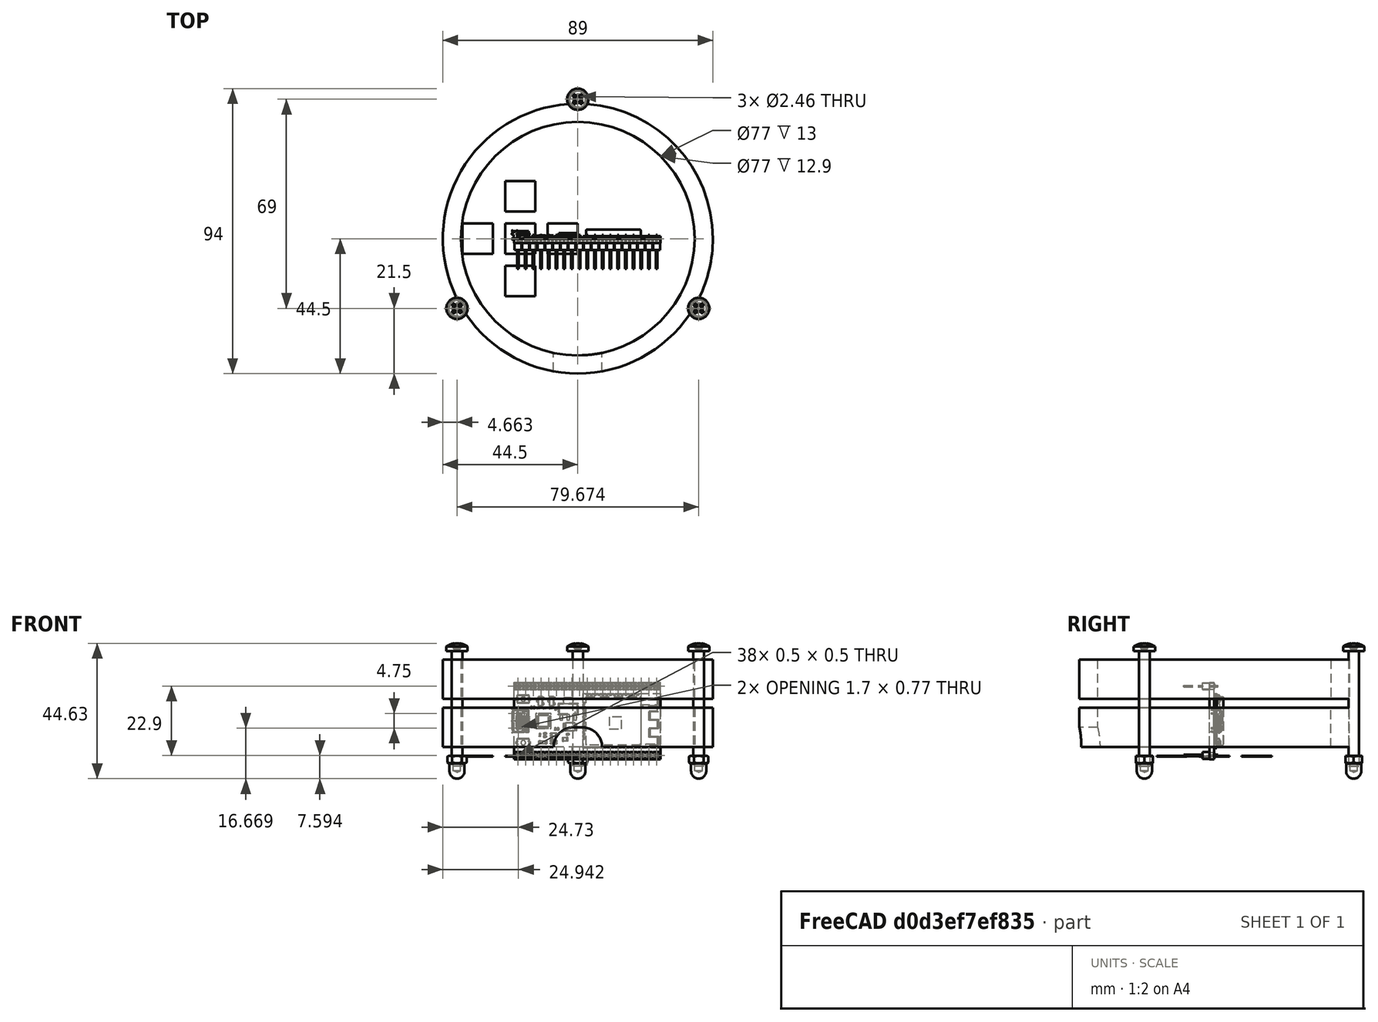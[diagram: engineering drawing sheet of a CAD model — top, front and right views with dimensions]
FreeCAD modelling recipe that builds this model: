
FCSTD DOCUMENT  (FreeCAD 2022.709R28846 (Git))
Label: infinity_02
License: Other
LicenseURL: https://ohwr.org/project/cernohl/wikis/Documents/CERN-OHL-version-2
objects: Part::Feature×98, TechDraw::DrawViewDimension×36, PartDesign::ShapeBinder×12, TechDraw::DrawProjGroupItem×12, Sketcher::SketchObject×10, App::DocumentObjectGroupPython×9, PartDesign::Body×8, TechDraw::DrawHatch×8, PartDesign::Plane×7, PartDesign::Pad×7, TechDraw::DrawSVGTemplate×7, TechDraw::DrawPage×7, TechDraw::DrawViewBalloon×7, Part::FeaturePython×6, TechDraw::DrawProjGroup×6, Part::Part2DObjectPython×4, App::DocumentObjectGroup×3, PartDesign::Pocket×2, Spreadsheet::Sheet×1, Part::Compound2×1, +1 more types
note: 172 computed .brp shape members not serialized (recipe doc carries the construction recipe); baked Part::Feature solids carry a one-line shape summary decoded from their .brp

FEATURE [Spreadsheet::Sheet] Spreadsheet
  PythonMode = false
  ShowCells = 0
  TreeRank = 0
  cells = B1=Enter board size values here manually; C1=NOTES; D1=Micro_Pro; E1=Nano; F1=ESP8266 NodeMCU; G1=ESP32 NodeMCU; H1=Add more boards; I1=Add more boards; A2=Length of the microcontroller board - choose from list (and add more as required); B2(Length)==48mm; D2==34mm; E2==47mm; F2==48mm; G2==48mm; A3=Width of the microcontroller board; B3(width)==26mm; D3==21mm; E3==21mm; F3==26mm; G3==26mm; A4=Screw hole diameter; B4(screw_hole_dia)==3mm; C4=Adds 0.2mm to screw hole diameter; A5=Main Inner circumference; B5(inner_circumference)==240mm; C5=for ESP32 IoT course, make this number divisible by 12 so that 12 LEDs can be placed around circumference for a future clock; A6=Acrylic Thickness; B6(acrylic_thickness)==2.9mm; A7=LED strip width; B7(led_strip_width)==10mm; C7=use this to adjust the height of the upper spacer
FEATURE [Sketcher::SketchObject] Sketch005
  ArcFitTolerance = 0
  AttachmentSupport = -> [XY_Plane010]
  FullyConstrained = true
  MapMode = 5
  Support = -> [XY_Plane010]
  TreeRank = 0
  expr: Constraints[1] = Spreadsheet.inner_circumference / 3.14159
  sketch-geometry (53):
    g0: Circle CenterX=0 CenterY=0 CenterZ=0 NormalX=0 NormalY=0 NormalZ=1 AngleXU=0 Radius=38.1972
    g1: Circle CenterX=0 CenterY=0 CenterZ=0 NormalX=0 NormalY=0 NormalZ=1 AngleXU=0 Radius=44.5
    g2: Circle CenterX=0 CenterY=0 CenterZ=0 NormalX=0 NormalY=0 NormalZ=1 AngleXU=0 Radius=50
    g3: Circle CenterX=0 CenterY=0 CenterZ=0 NormalX=0 NormalY=0 NormalZ=1 AngleXU=0 Radius=38.5
    g4: LineSegment StartX=38.2587 StartY=9.99981 StartZ=0 EndX=28.1331 EndY=27.7894 EndZ=0
    g5: LineSegment StartX=28.1331 StartY=27.7894 StartZ=0 EndX=10.4692 EndY=38.1329 EndZ=0
    g6: LineSegment StartX=10.4692 StartY=38.1329 StartZ=0 EndX=-9.99981 EndY=38.2587 EndZ=0
    g7: LineSegment StartX=-9.99981 StartY=38.2587 StartZ=0 EndX=-27.7894 EndY=28.1331 EndZ=0
    g8: LineSegment StartX=-27.7894 StartY=28.1331 StartZ=0 EndX=-38.1329 EndY=10.4692 EndZ=0
    g9: LineSegment StartX=-38.1329 StartY=10.4692 StartZ=0 EndX=-38.2587 EndY=-9.99981 EndZ=0
    g10: LineSegment StartX=-38.2587 StartY=-9.99981 StartZ=0 EndX=-28.1331 EndY=-27.7894 EndZ=0
    g11: LineSegment StartX=-28.1331 StartY=-27.7894 StartZ=0 EndX=-10.4692 EndY=-38.1329 EndZ=0
    g12: LineSegment StartX=-10.4692 StartY=-38.1329 StartZ=0 EndX=9.99981 EndY=-38.2587 EndZ=0
    g13: LineSegment StartX=9.99981 StartY=-38.2587 StartZ=0 EndX=27.7894 EndY=-28.1331 EndZ=0
    g14: LineSegment StartX=27.7894 StartY=-28.1331 StartZ=0 EndX=38.1329 EndY=-10.4692 EndZ=0
    g15: LineSegment StartX=38.1329 StartY=-10.4692 StartZ=0 EndX=38.2587 EndY=9.99981 EndZ=0
    g16: Circle [constr] CenterX=0 CenterY=0 CenterZ=0 NormalX=0 NormalY=0 NormalZ=1 AngleXU=0 Radius=39.5439
    g17: LineSegment StartX=0 StartY=0 StartZ=0 EndX=0 EndY=38.1972 EndZ=0
    g18: LineSegment StartX=0 StartY=0 StartZ=0 EndX=19.0986 EndY=33.0798 EndZ=0
    g19: LineSegment StartX=0 StartY=0 StartZ=0 EndX=33.0798 EndY=19.0986 EndZ=0
    g20: LineSegment StartX=0 StartY=0 StartZ=0 EndX=38.1972 EndY=3.5e-15 EndZ=0
    g21: LineSegment StartX=0 StartY=0 StartZ=0 EndX=33.0798 EndY=-19.0986 EndZ=0
    g22: LineSegment StartX=0 StartY=0 StartZ=0 EndX=19.0986 EndY=-33.0798 EndZ=0
    g23: LineSegment StartX=0 StartY=0 StartZ=0 EndX=1.85e-14 EndY=-38.1972 EndZ=0
    g24: LineSegment StartX=0 StartY=0 StartZ=0 EndX=-19.0986 EndY=-33.0798 EndZ=0
    g25: LineSegment StartX=0 StartY=0 StartZ=0 EndX=-33.0798 EndY=-19.0986 EndZ=0
    g26: LineSegment StartX=0 StartY=0 StartZ=0 EndX=-38.1972 EndY=-5.03e-14 EndZ=0
    g27: LineSegment StartX=0 StartY=0 StartZ=0 EndX=-33.0798 EndY=19.0986 EndZ=0
    g28: LineSegment StartX=0 StartY=0 StartZ=0 EndX=-19.0986 EndY=33.0798 EndZ=0
    g29: LineSegment StartX=0 StartY=0 StartZ=0 EndX=3.99992 EndY=38.1726 EndZ=0
    g30: LineSegment StartX=0 StartY=0 StartZ=0 EndX=-3.99992 EndY=38.2218 EndZ=0
    g31: LineSegment StartX=0 StartY=0 StartZ=0 EndX=15.6469 EndY=35.101 EndZ=0
    g32: LineSegment StartX=0 StartY=0 StartZ=0 EndX=22.5504 EndY=31.0585 EndZ=0
    g33: LineSegment StartX=0 StartY=0 StartZ=0 EndX=31.1011 EndY=22.5749 EndZ=0
    g34: LineSegment StartX=0 StartY=0 StartZ=0 EndX=35.0584 EndY=15.6223 EndZ=0
    g35: LineSegment StartX=0 StartY=0 StartZ=0 EndX=38.2218 EndY=3.99992 EndZ=0
    g36: LineSegment StartX=0 StartY=0 StartZ=0 EndX=38.1726 EndY=-3.99992 EndZ=0
    g37: LineSegment StartX=0 StartY=0 StartZ=0 EndX=35.101 EndY=-15.6469 EndZ=0
    g38: LineSegment StartX=0 StartY=0 StartZ=0 EndX=31.0585 EndY=-22.5504 EndZ=0
    g39: LineSegment StartX=0 StartY=0 StartZ=0 EndX=22.5749 EndY=-31.1011 EndZ=0
    g40: LineSegment StartX=0 StartY=0 StartZ=0 EndX=15.6223 EndY=-35.0584 EndZ=0
    g41: LineSegment StartX=0 StartY=0 StartZ=0 EndX=3.99992 EndY=-38.2218 EndZ=0
    g42: LineSegment StartX=0 StartY=0 StartZ=0 EndX=-3.99992 EndY=-38.1726 EndZ=0
    g43: LineSegment StartX=0 StartY=0 StartZ=0 EndX=-15.6469 EndY=-35.101 EndZ=0
    g44: LineSegment StartX=0 StartY=0 StartZ=0 EndX=-22.5504 EndY=-31.0585 EndZ=0
    g45: LineSegment StartX=0 StartY=0 StartZ=0 EndX=-31.1011 EndY=-22.5749 EndZ=0
    g46: LineSegment StartX=0 StartY=0 StartZ=0 EndX=-35.0584 EndY=-15.6223 EndZ=0
    g47: LineSegment StartX=0 StartY=0 StartZ=0 EndX=-38.2218 EndY=-3.99992 EndZ=0
    g48: LineSegment StartX=0 StartY=0 StartZ=0 EndX=-38.1726 EndY=3.99992 EndZ=0
    g49: LineSegment StartX=0 StartY=0 StartZ=0 EndX=-35.101 EndY=15.6469 EndZ=0
    g50: LineSegment StartX=0 StartY=0 StartZ=0 EndX=-31.0585 EndY=22.5504 EndZ=0
    g51: LineSegment StartX=0 StartY=0 StartZ=0 EndX=-22.5749 EndY=31.1011 EndZ=0
    g52: LineSegment StartX=0 StartY=0 StartZ=0 EndX=-15.6223 EndY=35.0584 EndZ=0
  constraints (143):
    c: Coincident(g0,g-1)
    c: Diameter(g0) = 76.3944
    c: Coincident(g1,g0)
    c: Diameter(g1) = 89
    c: Coincident(g2,g0)
    c: Diameter(g2) = 100
    c: Coincident(g3,g0)
    c: Diameter(g3) = 77
    c: Coincident(g4,g5)
    c: Coincident(g5,g6)
    c: Coincident(g6,g7)
    c: Coincident(g7,g8)
    c: Coincident(g8,g9)
    c: Coincident(g9,g10)
    c: Coincident(g10,g11)
    c: Coincident(g11,g12)
    c: Coincident(g12,g13)
    c: Coincident(g13,g14)
    c: Coincident(g14,g15)
    c: Coincident(g15,g4)
    c: Equal(g4, g5-g15) x11
    c: PointOnObject(g4,g16)
    c: PointOnObject(g5,g16)
    c: PointOnObject(g6,g16)
    c: PointOnObject(g7,g16)
    c: PointOnObject(g8,g16)
    c: PointOnObject(g9,g16)
    c: PointOnObject(g10,g16)
    c: PointOnObject(g11,g16)
    c: PointOnObject(g12,g16)
    c: PointOnObject(g13,g16)
    c: PointOnObject(g14,g16)
    c: Coincident(g16,g0)
    c: Coincident(g17,g0)
    c: PointOnObject(g17,g6)
    c: Distance(g17,g6) = 10
    c: Coincident(g18,g0)
    c: PointOnObject(g18,g5)
    c: Coincident(g19,g0)
    c: PointOnObject(g19,g4)
    c: Coincident(g20,g0)
    c: PointOnObject(g20,g15)
    c: Coincident(g21,g0)
    c: PointOnObject(g21,g14)
    c: Coincident(g22,g0)
    c: PointOnObject(g22,g13)
    c: Coincident(g23,g0)
    c: PointOnObject(g23,g12)
    c: Coincident(g24,g0)
    c: PointOnObject(g24,g11)
    c: Coincident(g25,g0)
    c: PointOnObject(g25,g10)
    c: Coincident(g26,g0)
    c: PointOnObject(g26,g9)
    c: Coincident(g27,g0)
    c: PointOnObject(g27,g8)
    c: Coincident(g28,g0)
    c: PointOnObject(g28,g7)
    c: Angle(g18,g17) = 0.523599
    c: Angle(g19,g18) = 0.523599
    c: Angle(g20,g19) = 0.523599
    c: Angle(g21,g20) = 0.523599
    c: Angle(g22,g21) = 0.523599
    c: Angle(g23,g22) = 0.523599
    c: Angle(g24,g23) = 0.523599
    c: Angle(g25,g24) = 0.523599
    c: Angle(g26,g25) = 0.523599
    c: Angle(g27,g26) = 0.523599
    c: Angle(g28,g27) = 0.523599
    c: PointOnObject(g4,g16)
    c: Vertical(g17)
    c: PointOnObject(g17,g0)
    c: Coincident(g29,g0)
    c: PointOnObject(g29,g6)
    c: Coincident(g30,g0)
    c: Symmetric(g30,g29,g17)
    c: Distance(g29,g30) = 8
    c: Coincident(g31,g0)
    c: PointOnObject(g31,g5)
    c: Coincident(g32,g0)
    c: PointOnObject(g32,g5)
    c: Angle(g31,g30) = 0.523599
    c: Angle(g32,g29) = 0.523599
    c: Coincident(g33,g0)
    c: PointOnObject(g33,g4)
    c: Coincident(g34,g0)
    c: PointOnObject(g34,g4)
    c: Angle(g33,g31) = 0.523599
    c: Angle(g34,g32) = 0.523599
    c: Coincident(g35,g0)
    c: PointOnObject(g35,g15)
    c: Coincident(g36,g0)
    c: PointOnObject(g36,g15)
    c: Angle(g35,g33) = 0.523599
    c: Angle(g36,g34) = 0.523599
    c: Coincident(g37,g0)
    c: PointOnObject(g37,g14)
    c: Coincident(g38,g0)
    c: PointOnObject(g38,g14)
    c: Angle(g37,g35) = 0.523599
    c: Angle(g38,g36) = 0.523599
    c: Coincident(g39,g0)
    c: PointOnObject(g39,g13)
    c: Coincident(g40,g0)
    c: PointOnObject(g40,g13)
    c: Angle(g39,g37) = 0.523599
    c: Angle(g40,g38) = 0.523599
    c: Coincident(g41,g0)
    c: PointOnObject(g41,g12)
    c: Coincident(g42,g0)
    c: PointOnObject(g42,g12)
    c: Angle(g41,g39) = 0.523599
    c: Angle(g42,g40) = 0.523599
    c: Coincident(g43,g0)
    c: PointOnObject(g43,g11)
    c: Coincident(g44,g0)
    c: PointOnObject(g44,g11)
    c: Angle(g43,g41) = 0.523599
    c: Angle(g44,g42) = 0.523599
    c: Coincident(g45,g0)
    c: PointOnObject(g45,g10)
    c: Coincident(g46,g0)
    c: PointOnObject(g46,g10)
    c: Angle(g45,g43) = 0.523599
    c: Angle(g46,g44) = 0.523599
    c: Coincident(g47,g0)
    c: PointOnObject(g47,g9)
    c: Coincident(g48,g0)
    c: PointOnObject(g48,g9)
    c: Angle(g47,g45) = 0.523599
    c: Angle(g48,g46) = 0.523599
    c: Coincident(g49,g0)
    c: PointOnObject(g49,g8)
    c: Coincident(g50,g0)
    c: PointOnObject(g50,g8)
    c: Angle(g49,g47) = 0.523599
    c: Angle(g50,g48) = 0.523599
    c: Coincident(g51,g0)
    c: PointOnObject(g51,g7)
    c: Coincident(g52,g0)
    c: PointOnObject(g52,g7)
    c: Angle(g51,g49) = 0.523599
    c: Angle(g52,g50) = 0.523599
FEATURE [PartDesign::Body] Body010
  AutoGroupSolids = false
  ClaimAllChildren = false
  ExportMode = 0
  Group = -> [Sketch005]
  Origin = -> Origin013
  TreeRank = 0
  _ExportChildren = -> [Sketch005]
  _GroupVersion = 1
FEATURE [PartDesign::ShapeBinder] ShapeBinder
  Support = -> [Sketch005]
  TraceSupport = false
  TreeRank = 0
FEATURE [PartDesign::Plane] DatumPlane
  AttachmentSupport = -> [ShapeBinder]
  Length = 10
  MapMode = 11
  MinimumLength = 10
  MinimumWidth = 10
  Placement = pos=(0,0,0) rot=(0,0,1;1.5708rad)
  ResizeMode = 0
  Support = -> [ShapeBinder]
  TreeRank = 0
  Width = 10
FEATURE [Sketcher::SketchObject] Sketch
  ArcFitTolerance = 0
  AttachmentSupport = -> [DatumPlane]
  ExternalGeometry = -> [ShapeBinder]
  FullyConstrained = true
  MapMode = 5
  Placement = pos=(0,0,0) rot=(0,0,1;1.5708rad)
  Support = -> [DatumPlane]
  TreeRank = 0
  sketch-geometry (2):
    g0: Circle CenterX=0 CenterY=0 CenterZ=0 NormalX=0 NormalY=0 NormalZ=1 AngleXU=0 Radius=44.5
    g1: Circle CenterX=0 CenterY=0 CenterZ=0 NormalX=0 NormalY=0 NormalZ=1 AngleXU=0 Radius=38.5
  constraints (4):
    c: Coincident(g0,g-4)
    c: Coincident(g1,g0)
    c: Equal(g1,g-4)
    c: Equal(g-3,g0)
FEATURE [PartDesign::Pad] Pad
  ClaimChildren = false
  Direction = (1,1,1)
  Fit = 0
  FitJoin = 0
  InnerFit = 0
  InnerFitJoin = 0
  InnerTaperAngle = 0
  InnerTaperAngleRev = 0
  Length = 5
  Length2 = 8
  NewSolid = false
  Placement = pos=(0,0,0) rot=(0,0,1;1.5708rad)
  Profile = -> Sketch
  Reversed = true
  Suppress = false
  TreeRank = 0
  Type = 4
  _ProfileBasedVersion = 0
FEATURE [PartDesign::Plane] DatumPlane002
  AttachmentOffset = pos=(0,0,0) rot=(1,0,0;1.5708rad)
  AttachmentSupport = -> [Pad]
  Length = 89
  MapMode = 45
  MinimumLength = 10
  MinimumWidth = 10
  Placement = pos=(3e-16,-1.42e-14,-1.5) rot=(1,0,0;1.5708rad)
  ResizeMode = 0
  Support = -> [Pad]
  TreeRank = 0
  Width = 13
FEATURE [Sketcher::SketchObject] Sketch007
  ArcFitTolerance = 0
  AttachmentSupport = -> [DatumPlane002]
  ExternalGeometry = -> [Pad]
  FullyConstrained = true
  MapMode = 5
  Placement = pos=(3e-16,-1.42e-14,-1.5) rot=(1,0,0;1.5708rad)
  Support = -> [DatumPlane002]
  TreeRank = 0
  sketch-geometry (4):
    g0: ArcOfCircle CenterX=-1.5 CenterY=-6.5 CenterZ=0 NormalX=0 NormalY=0 NormalZ=1 AngleXU=0 Radius=6.5 StartAngle=1.5708 EndAngle=4.71239
    g1: ArcOfCircle CenterX=1.5 CenterY=-6.5 CenterZ=0 NormalX=0 NormalY=0 NormalZ=1 AngleXU=0 Radius=6.5 StartAngle=4.71239 EndAngle=7.85398
    g2: LineSegment StartX=-1.5 StartY=-13 StartZ=0 EndX=1.5 EndY=-13 EndZ=0
    g3: LineSegment StartX=-1.5 StartY=9e-16 StartZ=0 EndX=1.5 EndY=1.8e-15 EndZ=0
  constraints (9):
    c: Tangent(g0,g3) = 1.5708
    c: Tangent(g0,g2) = -1.5708
    c: Tangent(g2,g1) = -1.5708
    c: Tangent(g3,g1) = 1.5708
    c: Horizontal(g2)
    c: DistanceX(g0,g1) = 3
    c: Symmetric(g1,g0,g-2)
    c: Radius(g0) = 6.5
    c: PointOnObject(g0,g-3)
FEATURE [PartDesign::Pocket] Pocket
  BaseFeature = -> Pad
  ClaimChildren = false
  Fit = 0
  FitJoin = 0
  InnerFit = 0
  InnerFitJoin = 0
  InnerTaperAngle = 0
  InnerTaperAngleRev = 0
  Length = 26
  Length2 = 100
  NewSolid = false
  Placement = pos=(0,0,0) rot=(0,0,1;1.5708rad)
  Profile = -> Sketch007
  Reversed = true
  Suppress = false
  TreeRank = 0
  Type = 1
  _ProfileBasedVersion = 0
FEATURE [PartDesign::Body] Body  label="PCB_lower_spacer"
  AutoGroupSolids = false
  ClaimAllChildren = false
  ExportMode = 0
  Group = -> [ShapeBinder,DatumPlane,Sketch,Pad,DatumPlane002,Sketch007,Pocket]
  Origin = -> Origin
  Tip = -> Pocket
  TreeRank = 0
  _ExportChildren = -> [ShapeBinder,DatumPlane,Pad,DatumPlane002,Pocket]
  _GroupVersion = 1
FEATURE [PartDesign::ShapeBinder] ShapeBinder002
  Support = -> [Sketch005]
  TraceSupport = false
  TreeRank = 0
FEATURE [PartDesign::ShapeBinder] ShapeBinder003
  Support = -> [Body]
  TraceSupport = false
  TreeRank = 0
FEATURE [PartDesign::Plane] DatumPlane004
  AttachmentSupport = -> [ShapeBinder003]
  Length = 100
  MapMode = 5
  MinimumLength = 10
  MinimumWidth = 10
  Placement = pos=(0,0,5) rot=(0,0,1;0rad)
  ResizeMode = 0
  Support = -> [ShapeBinder003]
  TreeRank = 0
  Width = 99.9333
FEATURE [Sketcher::SketchObject] Sketch009
  ArcFitTolerance = 0
  AttachmentSupport = -> [DatumPlane004]
  ExternalGeometry = -> [ShapeBinder002]
  FullyConstrained = true
  MapMode = 5
  Placement = pos=(0,0,5) rot=(0,0,1;0rad)
  Support = -> [DatumPlane004]
  TreeRank = 0
  expr: Constraints[1] = Spreadsheet.screw_hole_dia
  sketch-geometry (8):
    g0: Circle CenterX=0 CenterY=0 CenterZ=0 NormalX=0 NormalY=0 NormalZ=1 AngleXU=0 Radius=50
    g1: Circle CenterX=0 CenterY=46 CenterZ=0 NormalX=0 NormalY=0 NormalZ=1 AngleXU=0 Radius=1.5
    g2: Circle CenterX=-39.8372 CenterY=-23 CenterZ=0 NormalX=0 NormalY=0 NormalZ=1 AngleXU=0 Radius=1.5
    g3: Circle CenterX=39.8372 CenterY=-23 CenterZ=0 NormalX=0 NormalY=0 NormalZ=1 AngleXU=0 Radius=1.5
    g4: LineSegment [constr] StartX=0 StartY=46 StartZ=0 EndX=-39.8372 EndY=-23 EndZ=0
    g5: LineSegment [constr] StartX=-39.8372 StartY=-23 StartZ=0 EndX=39.8372 EndY=-23 EndZ=0
    g6: LineSegment [constr] StartX=39.8372 StartY=-23 StartZ=0 EndX=0 EndY=46 EndZ=0
    g7: Circle [constr] CenterX=0 CenterY=0 CenterZ=0 NormalX=0 NormalY=0 NormalZ=1 AngleXU=0 Radius=46
  constraints (19):
    c: Equal(g-3,g0)
    c: Diameter(g1) = 3
    c: Equal(g1,g2)
    c: Equal(g1,g3)
    c: PointOnObject(g1,g-2)
    c: Tangent(g1,g-5)
    c: Tangent(g2,g-5)
    c: Tangent(g3,g-5)
    c: Coincident(g4,g5)
    c: Coincident(g5,g6)
    c: Coincident(g6,g4)
    c: Equal(g4,g5)
    c: Equal(g4,g6)
    c: PointOnObject(g4,g7)
    c: Coincident(g6,g1)
    c: Coincident(g2,g4)
    c: Coincident(g3,g5)
    c: Coincident(g0,g-5)
    c: Coincident(g7,g0)
FEATURE [PartDesign::Pad] Pad002
  ClaimChildren = false
  Direction = (1,1,1)
  Fit = 0
  FitJoin = 0
  InnerFit = 0
  InnerFitJoin = 0
  InnerTaperAngle = 0
  InnerTaperAngleRev = 0
  Length = 2.9
  Length2 = 100
  NewSolid = false
  Placement = pos=(0,0,5) rot=(0,0,1;0rad)
  Profile = -> Sketch009
  Suppress = false
  TreeRank = 0
  Type = 0
  _ProfileBasedVersion = 0
  expr: Length = Spreadsheet.acrylic_thickness
FEATURE [Part::Feature] Solid089
  TreeRank = 0
  shape: bbox 0.66 x 0.051 x 0.304 mm, 6 faces (baked)
FEATURE [Part::Feature] Solid090
  TreeRank = 0
  shape: bbox 0.5016 x 0.5016 x 1 mm, 66 faces (baked)
FEATURE [Part::Feature] Solid091
  TreeRank = 0
  shape: bbox 0.66 x 0.051 x 0.304 mm, 6 faces (baked)
FEATURE [Part::Feature] Solid092
  TreeRank = 0
  shape: bbox 0.66 x 0.051 x 0.304 mm, 6 faces (baked)
FEATURE [Part::Feature] Solid093
  TreeRank = 0
  shape: bbox 1.02 x 0.52 x 0.52 mm, 15 faces (baked)
FEATURE [Part::Feature] Solid094
  TreeRank = 0
  shape: bbox 0.65 x 1.325 x 2.3 mm, 11 faces (baked)
FEATURE [Part::Feature] Solid095
  TreeRank = 0
  shape: bbox 2.126 x 0.2178 x 1.073 mm, 52 faces (baked)
FEATURE [Part::Feature] Solid096
  TreeRank = 0
  shape: bbox 0.4 x 0.2 x 0.8 mm, 8 faces (baked)
FEATURE [Part::Feature] Solid097
  TreeRank = 0
  shape: bbox 4.2 x 1.55 x 0.3 mm, 15 faces (baked)
FEATURE [Part::Feature] Solid098
  TreeRank = 0
  shape: bbox 1.624 x 0.5 x 1.624 mm, 6 faces (baked)
FEATURE [Part::Feature] Solid099
  TreeRank = 0
  shape: bbox 1.02 x 0.52 x 0.52 mm, 15 faces (baked)
FEATURE [Part::Feature] Solid100
  TreeRank = 0
  shape: bbox 1 x 0.5016 x 0.5016 mm, 66 faces (baked)
FEATURE [Part::Feature] Solid101
  TreeRank = 0
  shape: bbox 3.9 x 1.7 x 2.5 mm, 6 faces (baked)
FEATURE [Part::Feature] Solid102
  TreeRank = 0
  shape: bbox 0.4 x 0.2 x 0.8 mm, 8 faces (baked)
FEATURE [Part::Feature] Solid103
  TreeRank = 0
  shape: bbox 4.2 x 1.55 x 0.3 mm, 15 faces (baked)
FEATURE [Part::Feature] Solid104
  TreeRank = 0
  shape: bbox 4.2 x 1.55 x 0.3 mm, 15 faces (baked)
FEATURE [Part::Feature] Solid105
  TreeRank = 0
  shape: bbox 1 x 0.5016 x 0.5016 mm, 66 faces (baked)
FEATURE [Part::Feature] Solid106
  TreeRank = 0
  shape: bbox 6.707 x 1.804 x 3.709 mm, 14 faces (baked)
FEATURE [Part::Feature] Solid107
  TreeRank = 0
  shape: bbox 0.52 x 0.52 x 1.02 mm, 15 faces (baked)
FEATURE [Part::Feature] Solid108
  TreeRank = 0
  shape: bbox 2 x 0.8516 x 1.252 mm, 66 faces (baked)
FEATURE [Part::Feature] Solid109
  TreeRank = 0
  shape: bbox 1.624 x 0.5 x 1.624 mm, 6 faces (baked)
FEATURE [Part::Feature] Solid110
  TreeRank = 0
  shape: bbox 3.9 x 1.2 x 0.1 mm, 14 faces (baked)
FEATURE [Part::Feature] Solid111
  TreeRank = 0
  shape: bbox 0.8392 x 0.9032 x 1.792 mm, 14 faces (baked)
FEATURE [Part::Feature] Solid112
  TreeRank = 0
  shape: bbox 3.9 x 1.7 x 2.5 mm, 6 faces (baked)
FEATURE [Part::Feature] Solid113
  TreeRank = 0
  shape: bbox 2.5 x 1.11 x 3 mm, 49 faces (baked)
FEATURE [Part::Feature] Solid114
  TreeRank = 0
  shape: bbox 0.304 x 0.051 x 0.66 mm, 6 faces (baked)
FEATURE [Part::Feature] Solid115
  TreeRank = 0
  shape: bbox 1.333 x 0.3705 x 1.073 mm, 18 faces (baked)
FEATURE [Part::Feature] Solid116 .. Solid121  x6 (patterned run collapsed; names and placements below)
  TreeRank = 0
  shape: bbox 0.304 x 0.051 x 0.66 mm, 6 faces (baked)
FEATURE [Part::Feature] Solid122
  TreeRank = 0
  shape: bbox 0.66 x 0.051 x 0.304 mm, 6 faces (baked)
FEATURE [Part::Feature] Solid123
  TreeRank = 0
  shape: bbox 0.52 x 0.52 x 1.02 mm, 15 faces (baked)
FEATURE [Part::Feature] Solid124
  TreeRank = 0
  shape: bbox 0.66 x 0.051 x 0.304 mm, 6 faces (baked)
FEATURE [Part::Feature] Solid125
  TreeRank = 0
  shape: bbox 3.9 x 1.2 x 0.1 mm, 14 faces (baked)
FEATURE [Part::Feature] Solid126 .. Solid130  x5 (patterned run collapsed; names and placements below)
  TreeRank = 0
  shape: bbox 0.66 x 0.051 x 0.304 mm, 6 faces (baked)
FEATURE [Part::Feature] Solid131
  TreeRank = 0
  shape: bbox 4.16 x 2.41 x 6.91 mm, 176 faces (baked)
FEATURE [Part::Feature] Solid132
  TreeRank = 0
  shape: bbox 0.304 x 0.051 x 0.66 mm, 6 faces (baked)
FEATURE [Part::Feature] Solid133
  TreeRank = 0
  shape: bbox 0.4 x 0.2 x 0.8 mm, 8 faces (baked)
FEATURE [Part::Feature] Solid134 .. Solid138  x5 (patterned run collapsed; names and placements below)
  TreeRank = 0
  shape: bbox 0.304 x 0.051 x 0.66 mm, 6 faces (baked)
FEATURE [Part::Feature] Solid139
  TreeRank = 0
  shape: bbox 0.52 x 0.52 x 1.02 mm, 15 faces (baked)
FEATURE [Part::Feature] Solid140
  TreeRank = 0
  shape: bbox 0.304 x 0.051 x 0.66 mm, 6 faces (baked)
FEATURE [Part::Feature] Solid141
  TreeRank = 0
  shape: bbox 3.352 x 0.051 x 3.352 mm, 6 faces (baked)
FEATURE [Part::Feature] Solid142
  TreeRank = 0
  shape: bbox 1.65 x 1.05 x 1.05 mm, 14 faces (baked)
FEATURE [Part::Feature] Solid143
  TreeRank = 0
  shape: bbox 0.4875 x 0.5625 x 0.9375 mm, 11 faces (baked)
FEATURE [Part::Feature] Solid144
  TreeRank = 0
  shape: bbox 0.4 x 0.2 x 0.8 mm, 8 faces (baked)
FEATURE [Part::Feature] Solid145
  TreeRank = 0
  shape: bbox 1.333 x 0.3705 x 1.073 mm, 18 faces (baked)
FEATURE [Part::Feature] Solid146
  TreeRank = 0
  shape: bbox 0.4875 x 0.5625 x 0.9375 mm, 11 faces (baked)
FEATURE [Part::Feature] Solid147
  TreeRank = 0
  shape: bbox 1 x 0.5016 x 0.5016 mm, 66 faces (baked)
FEATURE [Part::Feature] Solid148
  TreeRank = 0
  shape: bbox 0.8392 x 0.9032 x 1.792 mm, 14 faces (baked)
FEATURE [Part::Feature] Solid149
  TreeRank = 0
  shape: bbox 1.02 x 0.52 x 0.52 mm, 15 faces (baked)
FEATURE [Part::Feature] Solid150
  TreeRank = 0
  shape: bbox 3.151 x 0.9032 x 1.792 mm, 14 faces (baked)
FEATURE [Part::Feature] Solid151
  TreeRank = 0
  shape: bbox 3.3 x 1.775 x 2.7 mm, 7 faces (baked)
FEATURE [Part::Feature] Solid152
  TreeRank = 0
  shape: bbox 0.65 x 1.325 x 2.3 mm, 11 faces (baked)
FEATURE [Part::Feature] Solid153
  TreeRank = 0
  shape: bbox 48.28 x 11.27 x 25.42 mm, 1344 faces (baked)
FEATURE [Part::Feature] Solid154
  TreeRank = 0
  shape: bbox 0.1854 x 0.003 x 0.1854 mm, 4 faces (baked)
FEATURE [Part::Feature] Solid155
  TreeRank = 0
  shape: bbox 2.126 x 0.2178 x 1.073 mm, 52 faces (baked)
FEATURE [Part::Feature] Solid156
  TreeRank = 0
  shape: bbox 4.2 x 1.55 x 0.3 mm, 15 faces (baked)
FEATURE [Part::Feature] Solid157
  TreeRank = 0
  shape: bbox 3.9 x 0.1 x 2.5 mm, 30 faces (baked)
FEATURE [Part::Feature] Solid158
  TreeRank = 0
  shape: bbox 0.52 x 0.52 x 1.02 mm, 15 faces (baked)
FEATURE [Part::Feature] Solid159
  TreeRank = 0
  shape: bbox 0.1 x 0.6 x 0.8 mm, 6 faces (baked)
FEATURE [Part::Feature] Solid160
  TreeRank = 0
  shape: bbox 2.5 x 1.11 x 3 mm, 49 faces (baked)
FEATURE [Part::Feature] Solid161
  TreeRank = 0
  shape: bbox 0.1 x 0.6 x 0.8 mm, 6 faces (baked)
FEATURE [Part::Feature] Solid162
  TreeRank = 0
  shape: bbox 3.9 x 1.2 x 0.1 mm, 14 faces (baked)
FEATURE [Part::Feature] Solid163
  TreeRank = 0
  shape: bbox 1.02 x 0.52 x 0.52 mm, 15 faces (baked)
FEATURE [Part::Feature] Solid164
  TreeRank = 0
  shape: bbox 5.63 x 3.797 x 8.183 mm, 257 faces (baked)
FEATURE [Part::Feature] Solid165
  TreeRank = 0
  shape: bbox 3.9 x 0.1 x 2.5 mm, 30 faces (baked)
FEATURE [Part::Feature] Solid166
  TreeRank = 0
  shape: bbox 4.2 x 1.55 x 0.3 mm, 15 faces (baked)
FEATURE [Part::Feature] Solid167
  TreeRank = 0
  shape: bbox 0.1 x 0.6 x 0.8 mm, 6 faces (baked)
FEATURE [Part::Feature] Solid168
  TreeRank = 0
  shape: bbox 0.1 x 0.6 x 0.8 mm, 6 faces (baked)
FEATURE [Part::Feature] Solid169
  TreeRank = 0
  shape: bbox 3.9 x 1.2 x 0.1 mm, 14 faces (baked)
FEATURE [Part::Feature] Solid170
  TreeRank = 0
  shape: bbox 0.52 x 0.52 x 1.02 mm, 15 faces (baked)
FEATURE [Part::Feature] Solid171
  TreeRank = 0
  shape: bbox 0.8392 x 0.9032 x 1.792 mm, 14 faces (baked)
FEATURE [Part::Feature] Solid172
  TreeRank = 0
  shape: bbox 0.2502 x 0.002 x 0.2502 mm, 4 faces (baked)
FEATURE [Part::Feature] Solid173
  TreeRank = 0
  shape: bbox 5.004 x 0.94 x 5.004 mm, 6 faces (baked)
FEATURE [Part::Feature] Solid174
  TreeRank = 0
  shape: bbox 0.66 x 0.051 x 0.304 mm, 6 faces (baked)
FEATURE [Part::Feature] Solid175
  TreeRank = 0
  shape: bbox 25.54 x 3.035 x 18.07 mm, 584 faces (baked)
FEATURE [Part::Feature] Solid176
  TreeRank = 0
  shape: bbox 0.66 x 0.051 x 0.304 mm, 6 faces (baked)
FEATURE [Part::Feature] Solid177
  TreeRank = 0
  shape: bbox 0.66 x 0.051 x 0.304 mm, 6 faces (baked)
FEATURE [Part::Feature] Solid178
  TreeRank = 0
  shape: bbox 0.66 x 0.051 x 0.304 mm, 6 faces (baked)
FEATURE [Part::Compound2] Compound001  label="ESP32Wroom4"
  Links = -> [Solid089,Solid090,Solid091,Solid092,Solid093,Solid094,Solid095,Solid096,Solid097,Solid098,Solid099,Solid100,Solid101,Solid102,Solid103,Solid104,Solid105,Solid106,Solid107,Solid108,Solid109,Solid110,Solid111,Solid112,Solid113,Solid114,Solid115,Solid116,Solid117,Solid118,Solid119,Solid120,Solid121,Solid122,Solid123,Solid124,Solid125,Solid126,Solid127,Solid128,Solid129,Solid130,Solid131,Solid132,+46 more]
  Placement = pos=(0.5,-15,-5) rot=(-0.57735,-0.57735,0.57735;2.0944rad)
  TreeRank = 0
FEATURE [Sketcher::SketchObject] Sketch010
  ArcFitTolerance = 0
  AttachmentSupport = -> [Pad002]
  ExternalGeometry = -> [ShapeBinder002]
  FullyConstrained = true
  MapMode = 5
  Placement = pos=(0,0,7.9) rot=(0,0,1;0rad)
  Support = -> [Pad002]
  TreeRank = 0
  sketch-geometry (5):
    g0: ArcOfCircle CenterX=-4 CenterY=-34.5 CenterZ=0 NormalX=0 NormalY=0 NormalZ=1 AngleXU=0 Radius=2 StartAngle=1.5708 EndAngle=4.71239
    g1: ArcOfCircle CenterX=4 CenterY=-34.5 CenterZ=0 NormalX=0 NormalY=0 NormalZ=1 AngleXU=0 Radius=2 StartAngle=4.71239 EndAngle=7.85398
    g2: LineSegment StartX=-4 StartY=-36.5 StartZ=0 EndX=4 EndY=-36.5 EndZ=0
    g3: LineSegment StartX=-4 StartY=-32.5 StartZ=0 EndX=4 EndY=-32.5 EndZ=0
    g4: LineSegment [constr] StartX=0 StartY=-38.5 StartZ=0 EndX=0 EndY=-36.5 EndZ=0
  constraints (13):
    c: Tangent(g0,g3) = 1.5708
    c: Tangent(g0,g2) = -1.5708
    c: Tangent(g2,g1) = -1.5708
    c: Tangent(g3,g1) = 1.5708
    c: Horizontal(g2)
    c: Diameter(g0) = 4
    c: Symmetric(g0,g1,g-2)
    c: DistanceX(g0,g1) = 8
    c: PointOnObject(g4,g-3)
    c: PointOnObject(g4,g2)
    c: Vertical(g4)
    c: PointOnObject(g4,g-2)
    c: DistanceY(g4,g4) = 2
FEATURE [PartDesign::Pocket] Pocket001
  BaseFeature = -> Pad002
  ClaimChildren = false
  Fit = 0
  FitJoin = 0
  InnerFit = 0
  InnerFitJoin = 0
  InnerTaperAngle = 0
  InnerTaperAngleRev = 0
  Length = 5
  Length2 = 100
  NewSolid = false
  Placement = pos=(0,0,5) rot=(0,0,1;0rad)
  Profile = -> Sketch010
  Suppress = false
  TreeRank = 0
  Type = 1
  _ProfileBasedVersion = 0
FEATURE [PartDesign::Body] Body012  label="Mirror"
  AutoGroupSolids = false
  ClaimAllChildren = false
  ExportMode = 0
  Group = -> [ShapeBinder002,ShapeBinder003,DatumPlane004,Sketch009,Pad002,Sketch010,Pocket001]
  Origin = -> Origin015
  Tip = -> Pocket001
  TreeRank = 0
  _ExportChildren = -> [ShapeBinder002,ShapeBinder003,DatumPlane004,Pad002,Pocket001]
  _GroupVersion = 1
FEATURE [PartDesign::ShapeBinder] ShapeBinder004 .. ShapeBinder007  x4 (patterned run collapsed; names and placements below)
  Support = -> [Sketch005]
  TraceSupport = false
  TreeRank = 0
FEATURE [PartDesign::Plane] DatumPlane008
  AttachmentSupport = -> [Pocket]
  Length = 98.9466
  MapMode = 5
  MinimumLength = 10
  MinimumWidth = 10
  Placement = pos=(0,0,-8) rot=(0.707107,0.707107,0;3.14159rad)
  ResizeMode = 0
  Support = -> [Pocket]
  TreeRank = 0
  Width = 99.95
FEATURE [Sketcher::SketchObject] Sketch014
  ArcFitTolerance = 0
  AttachmentSupport = -> [DatumPlane008]
  ExternalGeometry = -> [ShapeBinder007]
  FullyConstrained = true
  MapMode = 5
  Placement = pos=(0,0,-8) rot=(0.707107,0.707107,0;3.14159rad)
  Support = -> [DatumPlane008]
  TreeRank = 0
  expr: Constraints[2] = Spreadsheet.screw_hole_dia
  sketch-geometry (62):
    g0: ArcOfCircle CenterX=-7e-16 CenterY=7e-16 CenterZ=0 NormalX=0 NormalY=0 NormalZ=1 AngleXU=0 Radius=50 StartAngle=3.35146 EndAngle=9.21491
    g1: Circle CenterX=-23 CenterY=-39.8372 CenterZ=0 NormalX=0 NormalY=0 NormalZ=1 AngleXU=0 Radius=1.5
    g2: Circle CenterX=46 CenterY=0 CenterZ=0 NormalX=0 NormalY=0 NormalZ=1 AngleXU=0 Radius=1.5
    g3: Circle CenterX=-23 CenterY=39.8372 CenterZ=0 NormalX=0 NormalY=0 NormalZ=1 AngleXU=0 Radius=1.5
    g4: LineSegment [constr] StartX=-23 StartY=-39.8372 StartZ=0 EndX=46 EndY=0 EndZ=0
    g5: LineSegment [constr] StartX=46 StartY=0 StartZ=0 EndX=-23 EndY=39.8372 EndZ=0
    g6: LineSegment [constr] StartX=-23 StartY=39.8372 StartZ=0 EndX=-23 EndY=-39.8372 EndZ=0
    g7: Circle [constr] CenterX=-7e-16 CenterY=7e-16 CenterZ=0 NormalX=0 NormalY=0 NormalZ=1 AngleXU=0 Radius=46
    g8: ArcOfCircle CenterX=22 CenterY=0 CenterZ=0 NormalX=0 NormalY=0 NormalZ=1 AngleXU=0 Radius=6 StartAngle=0.523599 EndAngle=5.75959
    g9: ArcOfCircle CenterX=34 CenterY=0 CenterZ=0 NormalX=0 NormalY=0 NormalZ=1 AngleXU=0 Radius=2 StartAngle=4.71239 EndAngle=7.85398
    g10: LineSegment StartX=28.9282 StartY=-2 StartZ=0 EndX=34 EndY=-2 EndZ=0
    g11: LineSegment StartX=28.9282 StartY=2 StartZ=0 EndX=34 EndY=2 EndZ=0
    g12: ArcOfCircle CenterX=28.9282 CenterY=4 CenterZ=0 NormalX=0 NormalY=0 NormalZ=1 AngleXU=0 Radius=2 StartAngle=3.66519 EndAngle=4.71239
    g13: ArcOfCircle CenterX=28.9282 CenterY=-4 CenterZ=0 NormalX=0 NormalY=0 NormalZ=1 AngleXU=0 Radius=2 StartAngle=1.5708 EndAngle=2.61799
    g14: LineSegment [constr] StartX=-5 StartY=7e-16 StartZ=0 EndX=5 EndY=7e-16 EndZ=0
    g15: LineSegment [constr] StartX=5 StartY=7e-16 StartZ=0 EndX=5 EndY=-10 EndZ=0
    g16: LineSegment [constr] StartX=5 StartY=-10 StartZ=0 EndX=-5 EndY=-10 EndZ=0
    g17: LineSegment [constr] StartX=-5 StartY=-10 StartZ=0 EndX=-5 EndY=0 EndZ=0
    g18: LineSegment [constr] StartX=-19 StartY=-14 StartZ=0 EndX=-9 EndY=-14 EndZ=0
    g19: LineSegment [constr] StartX=-9 StartY=-14 StartZ=0 EndX=-9 EndY=-24 EndZ=0
    g20: LineSegment [constr] StartX=-9 StartY=-24 StartZ=0 EndX=-19 EndY=-24 EndZ=0
    g21: LineSegment [constr] StartX=-19 StartY=-24 StartZ=0 EndX=-19 EndY=-14 EndZ=0
    g22: LineSegment [constr] StartX=9 StartY=-14 StartZ=0 EndX=19 EndY=-14 EndZ=0
    g23: LineSegment [constr] StartX=19 StartY=-14 StartZ=0 EndX=19 EndY=-24 EndZ=0
    g24: LineSegment [constr] StartX=19 StartY=-24 StartZ=0 EndX=9 EndY=-24 EndZ=0
    g25: LineSegment [constr] StartX=9 StartY=-24 StartZ=0 EndX=9 EndY=-14 EndZ=0
    g26: LineSegment [constr] StartX=-5 StartY=-14 StartZ=0 EndX=5 EndY=-14 EndZ=0
    g27: LineSegment [constr] StartX=5 StartY=-14 StartZ=0 EndX=5 EndY=-24 EndZ=0
    g28: LineSegment [constr] StartX=5 StartY=-24 StartZ=0 EndX=-5 EndY=-24 EndZ=0
    g29: LineSegment [constr] StartX=-5 StartY=-24 StartZ=0 EndX=-5 EndY=-14 EndZ=0
    g30: LineSegment [constr] StartX=-5 StartY=-28 StartZ=0 EndX=5 EndY=-28 EndZ=0
    g31: LineSegment [constr] StartX=5 StartY=-28 StartZ=0 EndX=5 EndY=-38 EndZ=0
    g32: LineSegment [constr] StartX=5 StartY=-38 StartZ=0 EndX=-5 EndY=-38 EndZ=0
    g33: LineSegment [constr] StartX=-5 StartY=-38 StartZ=0 EndX=-5 EndY=-28 EndZ=0
    g34: LineSegment [constr] StartX=-5 StartY=-10 StartZ=0 EndX=-5 EndY=-14 EndZ=0
    g35: LineSegment [constr] StartX=-5 StartY=-14 StartZ=0 EndX=-9 EndY=-14 EndZ=0
    g36: LineSegment [constr] StartX=5 StartY=-10 StartZ=0 EndX=5 EndY=-14 EndZ=0
    g37: LineSegment [constr] StartX=5 StartY=-14 StartZ=0 EndX=9 EndY=-14 EndZ=0
    g38: LineSegment [constr] StartX=5 StartY=-28 StartZ=0 EndX=5 EndY=-24 EndZ=0
    g39: LineSegment [constr] StartX=5 StartY=-24 StartZ=0 EndX=9 EndY=-24 EndZ=0
    g40: LineSegment [constr] StartX=-5 StartY=-28 StartZ=0 EndX=-5 EndY=-24 EndZ=0
    g41: LineSegment [constr] StartX=-5 StartY=-24 StartZ=0 EndX=-9 EndY=-24 EndZ=0
    g42: LineSegment [constr] StartX=-7 StartY=-12 StartZ=0 EndX=7 EndY=-12 EndZ=0
    g43: LineSegment [constr] StartX=7 StartY=-12 StartZ=0 EndX=7 EndY=-26 EndZ=0
    g44: LineSegment [constr] StartX=7 StartY=-26 StartZ=0 EndX=-7 EndY=-26 EndZ=0
    g45: LineSegment [constr] StartX=-7 StartY=-26 StartZ=0 EndX=-7 EndY=-12 EndZ=0
    g46: LineSegment [constr] StartX=-1.3e-15 StartY=-12 StartZ=0 EndX=-1.3e-15 EndY=-26 EndZ=0
    g47: LineSegment [constr] StartX=7 StartY=-19 StartZ=0 EndX=-7 EndY=-19 EndZ=0
    g48: Circle CenterX=-7 CenterY=-12 CenterZ=0 NormalX=0 NormalY=0 NormalZ=1 AngleXU=0 Radius=1.5
    g49: Circle CenterX=-1.3e-15 CenterY=-12 CenterZ=0 NormalX=0 NormalY=0 NormalZ=1 AngleXU=0 Radius=1.5
    g50: Circle CenterX=7 CenterY=-12 CenterZ=0 NormalX=0 NormalY=0 NormalZ=1 AngleXU=0 Radius=1.5
    g51: Circle CenterX=7 CenterY=-19 CenterZ=0 NormalX=0 NormalY=0 NormalZ=1 AngleXU=0 Radius=1.5
    g52: Circle CenterX=7 CenterY=-26 CenterZ=0 NormalX=0 NormalY=0 NormalZ=1 AngleXU=0 Radius=1.5
    g53: Circle CenterX=-1.3e-15 CenterY=-26 CenterZ=0 NormalX=0 NormalY=0 NormalZ=1 AngleXU=0 Radius=1.5
    g54: Circle CenterX=-7 CenterY=-26 CenterZ=0 NormalX=0 NormalY=0 NormalZ=1 AngleXU=0 Radius=1.5
    g55: Circle CenterX=-7 CenterY=-19 CenterZ=0 NormalX=0 NormalY=0 NormalZ=1 AngleXU=0 Radius=1.5
    g56: ArcOfCircle CenterX=-36.9468 CenterY=1e-16 CenterZ=0 NormalX=0 NormalY=0 NormalZ=1 AngleXU=0 Radius=8 StartAngle=4.71239 EndAngle=7.85398
    g57: LineSegment StartX=-36.9468 StartY=8 StartZ=0 EndX=-46.9468 EndY=8 EndZ=0
    g58: LineSegment StartX=-36.9468 StartY=-8 StartZ=0 EndX=-46.9468 EndY=-8 EndZ=0
    g59: ArcOfCircle CenterX=-46.9468 CenterY=-10 CenterZ=0 NormalX=0 NormalY=0 NormalZ=1 AngleXU=0 Radius=2 StartAngle=1.5708 EndAngle=3.35146
    g60: ArcOfCircle CenterX=-46.9468 CenterY=10 CenterZ=0 NormalX=0 NormalY=0 NormalZ=1 AngleXU=0 Radius=2 StartAngle=2.93172 EndAngle=4.71239
    g61: LineSegment [constr] StartX=34 StartY=0 StartZ=0 EndX=46 EndY=0 EndZ=0
  constraints (155):
    c: Coincident(g0,g-3)
    c: Equal(g0,g-3)
    c: Diameter(g3) = 3
    c: Equal(g3,g2)
    c: Equal(g3,g1)
    c: Tangent(g1,g-4)
    c: Coincident(g4,g5)
    c: Coincident(g5,g6)
    c: Coincident(g6,g4)
    c: Equal(g4,g5)
    c: Equal(g4,g6)
    c: PointOnObject(g5,g7)
    c: Coincident(g6,g1)
    c: Coincident(g2,g4)
    c: Coincident(g3,g5)
    c: Coincident(g7,g0)
    c: Tangent(g10,g9) = -1.5708
    c: Tangent(g11,g9) = 1.5708
    c: Diameter(g9) = 4
    c: Diameter(g8) = 12
    c: Tangent(g8,g12) = 1.5708
    c: Tangent(g11,g12) = -1.5708
    c: Tangent(g8,g13) = 1.5708
    c: Tangent(g10,g13) = 1.5708
    c: Radius(g13) = 2
    c: Equal(g13,g12)
    c: Coincident(g14,g15)
    c: Coincident(g15,g16)
    c: Coincident(g16,g17)
    c: Coincident(g17,g14)
    c: Horizontal(g14)
    c: Horizontal(g16)
    c: Vertical(g15)
    c: Vertical(g17)
    c: Coincident(g18,g19)
    c: Coincident(g19,g20)
    c: Coincident(g20,g21)
    c: Coincident(g21,g18)
    c: Horizontal(g18)
    c: Horizontal(g20)
    c: Vertical(g19)
    c: Vertical(g21)
    c: Coincident(g22,g23)
    c: Coincident(g23,g24)
    c: Coincident(g24,g25)
    c: Coincident(g25,g22)
    c: Horizontal(g22)
    c: Horizontal(g24)
    c: Vertical(g23)
    c: Vertical(g25)
    c: Coincident(g26,g27)
    c: Coincident(g27,g28)
    c: Coincident(g28,g29)
    c: Coincident(g29,g26)
    c: Horizontal(g26)
    c: Horizontal(g28)
    c: Vertical(g27)
    c: Vertical(g29)
    c: Coincident(g30,g31)
    c: Coincident(g31,g32)
    c: Coincident(g32,g33)
    c: Coincident(g33,g30)
    c: Horizontal(g30)
    c: Horizontal(g32)
    c: Vertical(g31)
    c: Vertical(g33)
    c: Equal(g16,g15)
    c: Equal(g19,g20)
    c: Equal(g31,g32)
    c: Equal(g24,g23)
    c: Equal(g27,g28)
    c: Equal(g14,g18)
    c: Equal(g18,g30)
    c: Equal(g30,g22)
    c: Equal(g22,g26)
    c: DistanceX(g14,g14) = 10
    c: Vertical(g16,g26)
    c: Vertical(g28,g30)
    c: Horizontal(g26,g18)
    c: Horizontal(g26,g22)
    c: Coincident(g34,g16)
    c: Coincident(g34,g26)
    c: Coincident(g35,g26)
    c: Coincident(g35,g18)
    c: Coincident(g36,g15)
    c: Coincident(g36,g26)
    c: Coincident(g37,g26)
    c: Coincident(g37,g22)
    c: Coincident(g38,g30)
    c: Coincident(g38,g27)
    c: Coincident(g39,g27)
    c: Coincident(g39,g24)
    c: Coincident(g40,g30)
    c: Coincident(g40,g28)
    c: Coincident(g41,g28)
    c: Coincident(g41,g19)
    c: Equal(g34,g40)
    c: Equal(g35,g37)
    c: Equal(g35,g34)
    c: DistanceX(g35,g35) = 4
    c: Tangent(g2,g-4)
    c: Coincident(g42,g43)
    c: Coincident(g43,g44)
    c: Coincident(g44,g45)
    c: Coincident(g45,g42)
    c: Symmetric(g18,g26,g45)
    c: Symmetric(g26,g22,g43)
    c: Symmetric(g15,g26,g42)
    c: Symmetric(g27,g30,g44)
    c: PointOnObject(g46,g44)
    c: Vertical(g46)
    c: PointOnObject(g47,g45)
    c: Horizontal(g47)
    c: Symmetric(g42,g42,g46)
    c: Symmetric(g42,g43,g47)
    c: Coincident(g48,g42)
    c: Coincident(g49,g46)
    c: Coincident(g50,g42)
    c: Coincident(g51,g47)
    c: Coincident(g52,g43)
    c: Coincident(g53,g46)
    c: Coincident(g54,g44)
    c: Coincident(g55,g47)
    c: Equal(g54,g55)
    c: Equal(g55,g48)
    c: Equal(g48,g49)
    c: Equal(g49,g50)
    c: Equal(g50,g52)
    c: Equal(g52,g53)
    c: Equal(g53,g51)
    c: Diameter(g51) = 3
    c: Tangent(g56,g58) = 1.5708
    c: Tangent(g56,g57) = -1.5708
    c: Diameter(g56) = 16
    c: Tangent(g58,g59) = -1.5708
    c: Tangent(g0,g59) = -1.5708
    c: Tangent(g57,g60) = 1.5708
    c: Tangent(g0,g60) = -1.5708
    c: Radius(g60) = 2
    c: Equal(g60,g59)
    c: Tangent(g3,g-4)
    c: Equal(g11,g10)
    c: Parallel(g10,g11)
    c: Horizontal(g8,g9)
    c: Distance(g8,g9) = 12
    c: Coincident(g61,g9)
    c: PointOnObject(g61,g7)
    c: Horizontal(g61)
    c: Distance(g61) = 12
    c: PointOnObject(g9,g-1)
    c: Symmetric(g14,g14,g0)
    c: Parallel(g57,g58)
    c: Symmetric(g56,g56,g-1)
    c: DistanceX(g57,g57) = 10
    c: Horizontal(g9,g2)
FEATURE [PartDesign::Pad] Pad006
  ClaimChildren = false
  Direction = (1,1,1)
  Fit = 0
  FitJoin = 0
  InnerFit = 0
  InnerFitJoin = 0
  InnerTaperAngle = 0
  InnerTaperAngleRev = 0
  Length = 2.9
  Length2 = 100
  NewSolid = false
  Placement = pos=(0,0,-8) rot=(0.707107,0.707107,0;3.14159rad)
  Profile = -> Sketch014
  Suppress = false
  TreeRank = 0
  Type = 0
  _ProfileBasedVersion = 0
  expr: Length = Spreadsheet.acrylic_thickness
FEATURE [Part::FeaturePython] Screw  label="(M3.5)x38-Screw"  # Fasteners workbench fastener (typed FeaturePython)
  Placement = pos=(-39.8372,-23,23.7) rot=(0,0,1;0rad)
  TreeRank = 0
  baseObject = -> Body015 [Edge12]
  diameter = 5
  invert = false
  leftHanded = false
  length = 11
  lengthCustom = 38
  matchOuter = false
  offset = 0
  thread = false
  type = 40
FEATURE [Part::FeaturePython] Screw001  label="(M3.5)x38-Screw279"  # Fasteners workbench fastener (typed FeaturePython)
  Placement = pos=(39.8372,-23,23.7) rot=(0,0,1;0rad)
  TreeRank = 0
  baseObject = -> Body015 [Edge9]
  diameter = 5
  invert = false
  leftHanded = false
  length = 11
  lengthCustom = 38
  matchOuter = false
  offset = 0
  thread = false
  type = 40
FEATURE [Part::FeaturePython] Screw002  label="(M3.5)x38-Screw280"  # Fasteners workbench fastener (typed FeaturePython)
  Placement = pos=(0,46,23.7) rot=(0,0,1;0rad)
  TreeRank = 0
  baseObject = -> Body015 [Edge15]
  diameter = 5
  invert = false
  leftHanded = false
  length = 11
  lengthCustom = 38
  matchOuter = false
  offset = 0
  thread = false
  type = 40
FEATURE [Part::FeaturePython] Nut  label="M3-Nut"  # Fasteners workbench fastener (typed FeaturePython)
  Placement = pos=(-39.8372,-23,-10.9) rot=(-1,0,0;3.14159rad)
  TreeRank = 0
  baseObject = -> Body016 [Edge69]
  diameter = 1
  invert = false
  leftHanded = false
  matchOuter = false
  offset = 0
  thread = false
  type = 9
FEATURE [Part::FeaturePython] Nut001  label="M3-Nut433"  # Fasteners workbench fastener (typed FeaturePython)
  Placement = pos=(39.8372,-23,-10.9) rot=(-1,0,0;3.14159rad)
  TreeRank = 0
  baseObject = -> Body016 [Edge63]
  diameter = 1
  invert = false
  leftHanded = false
  matchOuter = false
  offset = 0
  thread = false
  type = 9
FEATURE [Part::FeaturePython] Nut002  label="M3-Nut434"  # Fasteners workbench fastener (typed FeaturePython)
  Placement = pos=(1e-14,46,-10.9) rot=(-1,0,0;3.14159rad)
  TreeRank = 0
  baseObject = -> Body016 [Edge66]
  diameter = 1
  invert = false
  leftHanded = false
  matchOuter = false
  offset = 0
  thread = false
  type = 9
FEATURE [PartDesign::ShapeBinder] ShapeBinder008
  Support = -> [Body012]
  TraceSupport = false
  TreeRank = 5
FEATURE [PartDesign::Plane] DatumPlane005
  AttachmentSupport = -> [ShapeBinder008]
  Length = 89
  MapMode = 5
  MinimumLength = 10
  MinimumWidth = 10
  Placement = pos=(0,0,7.9) rot=(0,0,1;0rad)
  ResizeMode = 0
  Support = -> [ShapeBinder008]
  TreeRank = 0
  Width = 89
FEATURE [Sketcher::SketchObject] Sketch011
  ArcFitTolerance = 0
  AttachmentSupport = -> [DatumPlane005]
  ExternalGeometry = -> [ShapeBinder004]
  FullyConstrained = true
  MapMode = 5
  Placement = pos=(0,0,7.9) rot=(0,0,1;0rad)
  Support = -> [DatumPlane005]
  TreeRank = 0
  sketch-geometry (2):
    g0: Circle CenterX=0 CenterY=0 CenterZ=0 NormalX=0 NormalY=0 NormalZ=1 AngleXU=0 Radius=44.5
    g1: Circle CenterX=0 CenterY=0 CenterZ=0 NormalX=0 NormalY=0 NormalZ=1 AngleXU=0 Radius=38.5
  constraints (4):
    c: Coincident(g0,g-4)
    c: Coincident(g1,g0)
    c: Equal(g1,g-4)
    c: Equal(g-3,g0)
FEATURE [PartDesign::Pad] Pad003
  ClaimChildren = false
  Direction = (1,1,1)
  Fit = 0
  FitJoin = 0
  InnerFit = 0
  InnerFitJoin = 0
  InnerTaperAngle = 0
  InnerTaperAngleRev = 0
  Length = 12.9
  Length2 = 100
  NewSolid = false
  Placement = pos=(0,0,7.9) rot=(0,0,1;0rad)
  Profile = -> Sketch011
  Suppress = false
  TreeRank = 0
  Type = 0
  _ProfileBasedVersion = 0
  expr: Length = Spreadsheet.led_strip_width + Spreadsheet.acrylic_thickness
FEATURE [PartDesign::Body] Body013  label="Upper_spacer"
  AutoGroupSolids = false
  ClaimAllChildren = false
  ExportMode = 0
  Group = -> [ShapeBinder004,DatumPlane005,Sketch011,Pad003,ShapeBinder008]
  Origin = -> Origin016
  Tip = -> Pad003
  TreeRank = 0
  _ExportChildren = -> [ShapeBinder004,DatumPlane005,Pad003,ShapeBinder008]
  _GroupVersion = 1
FEATURE [PartDesign::ShapeBinder] ShapeBinder009
  Support = -> [Body013]
  TraceSupport = false
  TreeRank = 6
FEATURE [PartDesign::Plane] DatumPlane006
  AttachmentSupport = -> [ShapeBinder009]
  Length = 77.4
  MapMode = 5
  MinimumLength = 10
  MinimumWidth = 10
  Placement = pos=(0,0,20.8) rot=(0,0,1;0rad)
  ResizeMode = 0
  Support = -> [ShapeBinder009]
  TreeRank = 0
  Width = 77.3484
FEATURE [Sketcher::SketchObject] Sketch012
  ArcFitTolerance = 0
  AttachmentSupport = -> [DatumPlane006]
  ExternalGeometry = -> [ShapeBinder005]
  FullyConstrained = true
  MapMode = 5
  Placement = pos=(0,0,20.8) rot=(0,0,1;0rad)
  Support = -> [DatumPlane006]
  TreeRank = 0
  sketch-geometry (2):
    g0: Circle CenterX=0 CenterY=0 CenterZ=0 NormalX=0 NormalY=0 NormalZ=1 AngleXU=0 Radius=38.7
    g1: LineSegment [constr] StartX=-38.7 StartY=0 StartZ=0 EndX=-38.5 EndY=0 EndZ=0
  constraints (6):
    c: Coincident(g0,g-3)
    c: PointOnObject(g1,g0)
    c: PointOnObject(g1,g-3)
    c: Horizontal(g1)
    c: PointOnObject(g1,g-1)
    c: DistanceX(g1,g1) = 0.2
FEATURE [PartDesign::Pad] Pad004
  ClaimChildren = false
  Direction = (1,1,1)
  Fit = 0
  FitJoin = 0
  InnerFit = 0
  InnerFitJoin = 0
  InnerTaperAngle = 0
  InnerTaperAngleRev = 0
  Length = 2.9
  Length2 = 100
  NewSolid = false
  Placement = pos=(0,0,20.8) rot=(0,0,1;0rad)
  Profile = -> Sketch012
  Reversed = true
  Suppress = false
  TreeRank = 0
  Type = 0
  _ProfileBasedVersion = 0
  expr: Length = Spreadsheet.acrylic_thickness
FEATURE [PartDesign::Body] Body014  label="Mirror_one_way"
  AutoGroupSolids = false
  ClaimAllChildren = false
  ExportMode = 0
  Group = -> [ShapeBinder005,DatumPlane006,Sketch012,Pad004,ShapeBinder009]
  Origin = -> Origin017
  Tip = -> Pad004
  TreeRank = 0
  _ExportChildren = -> [ShapeBinder005,DatumPlane006,Pad004,ShapeBinder009]
  _GroupVersion = 1
FEATURE [PartDesign::ShapeBinder] ShapeBinder010
  Support = -> [Body013]
  TraceSupport = false
  TreeRank = 7
FEATURE [PartDesign::Plane] DatumPlane007
  AttachmentSupport = -> [ShapeBinder010]
  Length = 100
  MapMode = 5
  MinimumLength = 10
  MinimumWidth = 10
  Placement = pos=(0,0,20.8) rot=(0,0,1;0rad)
  ResizeMode = 0
  Support = -> [ShapeBinder010]
  TreeRank = 0
  Width = 99.9333
FEATURE [Sketcher::SketchObject] Sketch013
  ArcFitTolerance = 0
  AttachmentSupport = -> [DatumPlane007]
  ExternalGeometry = -> [ShapeBinder006]
  FullyConstrained = true
  MapMode = 5
  Placement = pos=(0,0,20.8) rot=(0,0,1;0rad)
  Support = -> [DatumPlane007]
  TreeRank = 0
  expr: Constraints[8] = Spreadsheet.screw_hole_dia
  sketch-geometry (10):
    g0: Circle CenterX=0 CenterY=0 CenterZ=0 NormalX=0 NormalY=0 NormalZ=1 AngleXU=0 Radius=50
    g1: Circle CenterX=0 CenterY=0 CenterZ=0 NormalX=0 NormalY=0 NormalZ=1 AngleXU=0 Radius=37
    g2: LineSegment [constr] StartX=-37 StartY=0 StartZ=0 EndX=-38.5 EndY=0 EndZ=0
    g3: Circle CenterX=0 CenterY=46 CenterZ=0 NormalX=0 NormalY=0 NormalZ=1 AngleXU=0 Radius=1.5
    g4: Circle CenterX=-39.8372 CenterY=-23 CenterZ=0 NormalX=0 NormalY=0 NormalZ=1 AngleXU=0 Radius=1.5
    g5: Circle CenterX=39.8372 CenterY=-23 CenterZ=0 NormalX=0 NormalY=0 NormalZ=1 AngleXU=0 Radius=1.5
    g6: LineSegment [constr] StartX=0 StartY=46 StartZ=0 EndX=-39.8372 EndY=-23 EndZ=0
    g7: LineSegment [constr] StartX=-39.8372 StartY=-23 StartZ=0 EndX=39.8372 EndY=-23 EndZ=0
    g8: LineSegment [constr] StartX=39.8372 StartY=-23 StartZ=0 EndX=0 EndY=46 EndZ=0
    g9: Circle [constr] CenterX=0 CenterY=0 CenterZ=0 NormalX=0 NormalY=0 NormalZ=1 AngleXU=0 Radius=46
  constraints (25):
    c: Coincident(g0,g-4)
    c: Coincident(g1,g0)
    c: Equal(g-3,g0)
    c: PointOnObject(g2,g1)
    c: PointOnObject(g2,g-4)
    c: Horizontal(g2)
    c: PointOnObject(g2,g-1)
    c: DistanceX(g2,g2) = 1.5
    c: Diameter(g4) = 3
    c: Equal(g4,g5)
    c: Equal(g4,g3)
    c: PointOnObject(g3,g-2)
    c: Tangent(g3,g-5)
    c: Coincident(g6,g7)
    c: Coincident(g7,g8)
    c: Coincident(g8,g6)
    c: Equal(g6,g7)
    c: Equal(g6,g8)
    c: PointOnObject(g6,g9)
    c: PointOnObject(g7,g9)
    c: PointOnObject(g8,g9)
    c: Coincident(g9,g0)
    c: Coincident(g8,g3)
    c: Coincident(g4,g6)
    c: Coincident(g5,g7)
FEATURE [PartDesign::Pad] Pad005
  ClaimChildren = false
  Direction = (1,1,1)
  Fit = 0
  FitJoin = 0
  InnerFit = 0
  InnerFitJoin = 0
  InnerTaperAngle = 0
  InnerTaperAngleRev = 0
  Length = 2.9
  Length2 = 100
  NewSolid = false
  Placement = pos=(0,0,20.8) rot=(0,0,1;0rad)
  Profile = -> Sketch013
  Suppress = false
  TreeRank = 0
  Type = 0
  _ProfileBasedVersion = 0
  expr: Length = Spreadsheet.acrylic_thickness
FEATURE [PartDesign::Body] Body015  label="Front_bezel"
  AutoGroupSolids = false
  ClaimAllChildren = false
  ExportMode = 0
  Group = -> [ShapeBinder006,DatumPlane007,Sketch013,Pad005,ShapeBinder010]
  Origin = -> Origin018
  Tip = -> Pad005
  TreeRank = 0
  _ExportChildren = -> [ShapeBinder006,DatumPlane007,Pad005,ShapeBinder010]
  _GroupVersion = 1
FEATURE [PartDesign::ShapeBinder] ShapeBinder011
  Support = -> [Body]
  TraceSupport = false
  TreeRank = 8
FEATURE [PartDesign::Body] Body016  label="Back_cover"
  AutoGroupSolids = false
  ClaimAllChildren = false
  ExportMode = 0
  Group = -> [ShapeBinder007,DatumPlane008,Sketch014,Pad006,ShapeBinder011]
  Origin = -> Origin019
  Tip = -> Pad006
  TreeRank = 0
  _ExportChildren = -> [ShapeBinder007,DatumPlane008,Pad006,ShapeBinder011]
  _GroupVersion = 1
FEATURE [Part::Part2DObjectPython] Shape2DView  label="Back_cover_DXF"  # Draft 2D object (typed FeaturePython)
  Base = -> Body016
  FuseArch = false
  HiddenLines = false
  InPlace = true
  Projection = (0,0,1)
  ProjectionMode = 0
  SegmentLength = 0.05
  Tessellation = false
  TreeRank = 9
  VisibleOnly = false
FEATURE [Part::Part2DObjectPython] Shape2DView001  label="Front_bezel_DXF"  # Draft 2D object (typed FeaturePython)
  Base = -> Body015
  FuseArch = false
  HiddenLines = false
  InPlace = true
  Projection = (0,0,1)
  ProjectionMode = 0
  SegmentLength = 0.05
  Tessellation = false
  TreeRank = 10
  VisibleOnly = false
FEATURE [Part::Part2DObjectPython] Shape2DView002  label="Mirror_one_way_DXF"  # Draft 2D object (typed FeaturePython)
  Base = -> Body014
  FuseArch = false
  HiddenLines = false
  InPlace = true
  Projection = (0,0,1)
  ProjectionMode = 0
  SegmentLength = 0.05
  Tessellation = false
  TreeRank = 11
  VisibleOnly = false
FEATURE [Part::Part2DObjectPython] Shape2DView003  label="Mirror_DXF"  # Draft 2D object (typed FeaturePython)
  Base = -> Body012
  FuseArch = false
  HiddenLines = false
  InPlace = true
  Projection = (0,0,1)
  ProjectionMode = 0
  SegmentLength = 0.05
  Tessellation = false
  TreeRank = 12
  VisibleOnly = false
FEATURE [App::DocumentObjectGroup] Group  label="DXF"
  ClaimAllChildren = true
  ExportMode = 1
  Group = -> [Shape2DView,Shape2DView001,Shape2DView002,Shape2DView003]
  TreeRank = 0
  _GroupVersion = 1
FEATURE [TechDraw::DrawSVGTemplate] Template
  EditableTexts = AUTHOR_NAME=Anool J M,DRAWING_TITLE=Lower Spacer,FC-DATE=02/04/2023,FC-REV=REV A,FC-SC=1:1,FC-SH=1 / 8,FC-SI=A4,FREECAD_DRAWING=77 mm ID, 89 mm OD,+3 more (map truncated)
  Height = 210
  Orientation = 1
  TreeRank = 14
  Width = 297
FEATURE [TechDraw::DrawSVGTemplate] Template001
  EditableTexts = AUTHOR_NAME=Anool J M,DRAWING_TITLE=Upper Spacer,FC-DATE=02/04/2023,FC-REV=REV A,FC-SC=1:1,FC-SH=2 / 8,FC-SI=A4,FREECAD_DRAWING=77 mm ID, 89 mm OD,+3 more (map truncated)
  Height = 210
  Orientation = 1
  TreeRank = 21
  Width = 297
FEATURE [TechDraw::DrawProjGroupItem] ProjItem002  label="Front001"
  CoarseView = false
  Direction = (0,0,1)
  Focus = 100
  HardHidden = true
  IsoCount = 0
  IsoHidden = false
  IsoVisible = false
  LockPosition = true
  Perspective = false
  Rotation = 0
  RotationVector = (1,0,0)
  ScaleType = 2
  SeamHidden = false
  SeamVisible = false
  SmoothHidden = false
  SmoothVisible = true
  Source = -> [Body013]
  TreeRank = 24
  Type = 0
  X = 0
  XDirection = (1,0,0)
  Y = 0
FEATURE [TechDraw::DrawProjGroupItem] ProjItem003  label="Bottom001"
  CoarseView = false
  Direction = (0,-1,0)
  Focus = 100
  HardHidden = true
  IsoCount = 0
  IsoHidden = false
  IsoVisible = false
  LockPosition = false
  Perspective = false
  Rotation = 0
  RotationVector = (1,0,0)
  ScaleType = 2
  SeamHidden = false
  SeamVisible = false
  SmoothHidden = false
  SmoothVisible = true
  Source = -> [Body013]
  TreeRank = 26
  Type = 5
  X = 0
  XDirection = (1,0,0)
  Y = 65.95
FEATURE [TechDraw::DrawProjGroup] ProjGroup001
  Anchor = -> ProjItem002
  AutoDistribute = true
  LockPosition = false
  ProjectionType = 0
  Rotation = 0
  ScaleType = 0
  Source = -> [Body013]
  TreeRank = 25
  Views = -> [ProjItem002,ProjItem003]
  X = 152.158
  Y = 100.518
  spacingX = 15
  spacingY = 15
FEATURE [TechDraw::DrawSVGTemplate] Template002
  EditableTexts = AUTHOR_NAME=Anool J M,DRAWING_TITLE=Mirror, 100%,FC-DATE=02/04/2023,FC-REV=REV A,FC-SC=1:1,FC-SH=3 / 8,FC-SI=A4,FREECAD_DRAWING=100 mm OD,+3 more (map truncated)
  Height = 210
  Orientation = 1
  TreeRank = 28
  Width = 297
FEATURE [TechDraw::DrawProjGroupItem] ProjItem004  label="Front002"
  CoarseView = false
  Direction = (0,0,1)
  Focus = 100
  HardHidden = true
  IsoCount = 0
  IsoHidden = false
  IsoVisible = false
  LockPosition = true
  Perspective = false
  Rotation = 0
  RotationVector = (1,0,0)
  ScaleType = 2
  SeamHidden = false
  SeamVisible = false
  SmoothHidden = false
  SmoothVisible = true
  Source = -> [Body012]
  TreeRank = 31
  Type = 0
  X = 0
  XDirection = (1,0,0)
  Y = 0
FEATURE [TechDraw::DrawProjGroupItem] ProjItem005  label="Right"
  CoarseView = false
  Direction = (1,0,1e-16)
  Focus = 100
  HardHidden = true
  IsoCount = 0
  IsoHidden = false
  IsoVisible = false
  LockPosition = false
  Perspective = false
  Rotation = 0
  RotationVector = (1,0,0)
  ScaleType = 2
  SeamHidden = false
  SeamVisible = false
  SmoothHidden = false
  SmoothVisible = true
  Source = -> [Body012]
  TreeRank = 33
  Type = 2
  X = -66.45
  XDirection = (1e-16,0,-1)
  Y = 0
FEATURE [TechDraw::DrawProjGroup] ProjGroup002
  Anchor = -> ProjItem004
  AutoDistribute = true
  LockPosition = false
  ProjectionType = 0
  Rotation = 0
  ScaleType = 0
  Source = -> [Body012]
  TreeRank = 32
  Views = -> [ProjItem004,ProjItem005]
  X = 103.115
  Y = 122.909
  spacingX = 15
  spacingY = 15
FEATURE [TechDraw::DrawSVGTemplate] Template003
  EditableTexts = AUTHOR_NAME=Anool J M,DRAWING_TITLE=Mirror, one way,FC-DATE=02/04/2023,FC-REV=REV A,FC-SC=1:1,FC-SH=4 / 8,FC-SI=A4,FREECAD_DRAWING=77.4 mm dia,+3 more (map truncated)
  Height = 210
  Orientation = 1
  TreeRank = 35
  Width = 297
FEATURE [TechDraw::DrawProjGroupItem] ProjItem006  label="Front003"
  CoarseView = false
  Direction = (0,0,1)
  Focus = 100
  HardHidden = true
  IsoCount = 0
  IsoHidden = false
  IsoVisible = false
  LockPosition = true
  Perspective = false
  Rotation = 0
  RotationVector = (1,0,0)
  ScaleType = 2
  SeamHidden = false
  SeamVisible = false
  SmoothHidden = false
  SmoothVisible = true
  Source = -> [Body014]
  TreeRank = 38
  Type = 0
  X = 0
  XDirection = (1,0,0)
  Y = 0
FEATURE [TechDraw::DrawProjGroupItem] ProjItem007  label="Right001"
  CoarseView = false
  Direction = (1,0,1e-16)
  Focus = 100
  HardHidden = true
  IsoCount = 0
  IsoHidden = false
  IsoVisible = false
  LockPosition = false
  Perspective = false
  Rotation = 0
  RotationVector = (1,0,0)
  ScaleType = 2
  SeamHidden = false
  SeamVisible = false
  SmoothHidden = false
  SmoothVisible = true
  Source = -> [Body014]
  TreeRank = 40
  Type = 2
  X = -55.15
  XDirection = (1e-16,0,-1)
  Y = 0
FEATURE [TechDraw::DrawProjGroup] ProjGroup003
  Anchor = -> ProjItem006
  AutoDistribute = true
  LockPosition = false
  ProjectionType = 0
  Rotation = 0
  ScaleType = 0
  Source = -> [Body014]
  TreeRank = 39
  Views = -> [ProjItem006,ProjItem007]
  X = 96.828
  Y = 129.074
  spacingX = 15
  spacingY = 15
FEATURE [TechDraw::DrawSVGTemplate] Template004
  EditableTexts = AUTHOR_NAME=Anool J M,DRAWING_TITLE=Front bezel,FC-DATE=02/04/2023,FC-REV=REV A,FC-SC=1:1,FC-SH=5 / 8,FC-SI=A4,FREECAD_DRAWING=100 mm OD, 74 mm ID,+3 more (map truncated)
  Height = 210
  Orientation = 1
  TreeRank = 42
  Width = 297
FEATURE [TechDraw::DrawProjGroupItem] ProjItem008  label="Front004"
  CoarseView = false
  Direction = (0,0,1)
  Focus = 100
  HardHidden = true
  IsoCount = 0
  IsoHidden = false
  IsoVisible = false
  LockPosition = true
  Perspective = false
  Rotation = 0
  RotationVector = (1,0,0)
  ScaleType = 2
  SeamHidden = false
  SeamVisible = false
  SmoothHidden = false
  SmoothVisible = true
  Source = -> [Body015]
  TreeRank = 45
  Type = 0
  X = 0
  XDirection = (1,0,0)
  Y = 0
FEATURE [TechDraw::DrawProjGroupItem] ProjItem009  label="Right002"
  CoarseView = false
  Direction = (1,0,1e-16)
  Focus = 100
  HardHidden = true
  IsoCount = 0
  IsoHidden = false
  IsoVisible = false
  LockPosition = false
  Perspective = false
  Rotation = 0
  RotationVector = (1,0,0)
  ScaleType = 2
  SeamHidden = false
  SeamVisible = false
  SmoothHidden = false
  SmoothVisible = true
  Source = -> [Body015]
  TreeRank = 47
  Type = 2
  X = -66.45
  XDirection = (1e-16,0,-1)
  Y = 0
FEATURE [TechDraw::DrawProjGroup] ProjGroup004
  Anchor = -> ProjItem008
  AutoDistribute = true
  LockPosition = false
  ProjectionType = 0
  Rotation = 0
  ScaleType = 0
  Source = -> [Body015]
  TreeRank = 46
  Views = -> [ProjItem008,ProjItem009]
  X = 107.394
  Y = 122.209
  spacingX = 15
  spacingY = 15
FEATURE [TechDraw::DrawSVGTemplate] Template005
  EditableTexts = AUTHOR_NAME=Anool J M,DRAWING_TITLE=Back cover,FC-DATE=02/04/2023,FC-REV=REV A,FC-SC=1:1,FC-SH=6 / 8,FC-SI=A4,FREECAD_DRAWING=100 mm OD,+3 more (map truncated)
  Height = 210
  Orientation = 1
  TreeRank = 49
  Width = 297
FEATURE [TechDraw::DrawProjGroupItem] ProjItem010  label="Front005"
  CoarseView = false
  Direction = (0,0,1)
  Focus = 100
  HardHidden = true
  IsoCount = 0
  IsoHidden = false
  IsoVisible = false
  LockPosition = true
  Perspective = false
  Rotation = 0
  RotationVector = (1,0,0)
  ScaleType = 2
  SeamHidden = false
  SeamVisible = false
  SmoothHidden = false
  SmoothVisible = true
  Source = -> [Body016]
  TreeRank = 52
  Type = 0
  X = 0
  XDirection = (1,0,0)
  Y = 0
FEATURE [TechDraw::DrawProjGroupItem] ProjItem011  label="Right003"
  CoarseView = false
  Direction = (1,0,1e-16)
  Focus = 100
  HardHidden = true
  IsoCount = 0
  IsoHidden = false
  IsoVisible = false
  LockPosition = false
  Perspective = false
  Rotation = 0
  RotationVector = (1,0,0)
  ScaleType = 2
  SeamHidden = false
  SeamVisible = false
  SmoothHidden = false
  SmoothVisible = true
  Source = -> [Body016]
  TreeRank = 54
  Type = 2
  X = -66.45
  XDirection = (1e-16,0,-1)
  Y = 0
FEATURE [TechDraw::DrawProjGroup] ProjGroup005
  Anchor = -> ProjItem010
  AutoDistribute = true
  LockPosition = false
  ProjectionType = 0
  Rotation = 0
  ScaleType = 0
  Source = -> [Body016]
  TreeRank = 53
  Views = -> [ProjItem010,ProjItem011]
  X = 104.78
  Y = 122.454
  spacingX = 15
  spacingY = 15
FEATURE [TechDraw::DrawViewDimension] Dimension004
  Arbitrary = false
  ArbitraryTolerances = false
  EqualTolerance = true
  FormatSpec = ⌀%.1f
  FormatSpecOverTolerance = %+.1f
  FormatSpecUnderTolerance = %+.1f
  Inverted = false
  LockPosition = false
  MeasureType = 1
  OverTolerance = 0
  References2D = -> [ProjItem002]
  Rotation = 0
  ScaleType = 0
  TheoreticalExact = false
  TreeRank = 59
  Type = 5
  UnderTolerance = 0
  X = 63.4264
  Y = 13.8579
FEATURE [TechDraw::DrawViewDimension] Dimension006
  Arbitrary = false
  ArbitraryTolerances = false
  EqualTolerance = true
  FormatSpec = ⌀%.1f
  FormatSpecOverTolerance = %+.1f
  FormatSpecUnderTolerance = %+.1f
  Inverted = false
  LockPosition = false
  MeasureType = 1
  OverTolerance = 0
  References2D = -> [ProjItem002]
  Rotation = 0
  ScaleType = 0
  TheoreticalExact = false
  TreeRank = 61
  Type = 5
  UnderTolerance = 0
  X = 65.5584
  Y = -11.4594
FEATURE [TechDraw::DrawViewDimension] Dimension007
  Arbitrary = false
  ArbitraryTolerances = false
  EqualTolerance = true
  FormatSpec = %.1f
  FormatSpecOverTolerance = %+.1f
  FormatSpecUnderTolerance = %+.1f
  Inverted = false
  LockPosition = false
  MeasureType = 1
  OverTolerance = 0
  References2D = -> [ProjItem003]
  Rotation = 0
  ScaleType = 0
  TheoreticalExact = false
  TreeRank = 62
  Type = 2
  UnderTolerance = 0
  X = 69.114
  Y = -15.3606
FEATURE [TechDraw::DrawPage] Page001
  KeepUpdated = true
  NextBalloonIndex = 1
  ProjectionType = 0
  Template = -> Template001
  TreeRank = 22
  Views = -> [ProjGroup001,Dimension004,Dimension006,Dimension007]
FEATURE [TechDraw::DrawViewDimension] Dimension008
  Arbitrary = false
  ArbitraryTolerances = false
  EqualTolerance = true
  FormatSpec = ⌀%.1f
  FormatSpecOverTolerance = %+.1f
  FormatSpecUnderTolerance = %+.1f
  Inverted = false
  LockPosition = false
  MeasureType = 1
  OverTolerance = 0
  References2D = -> [ProjItem004]
  Rotation = 0
  ScaleType = 0
  TheoreticalExact = false
  TreeRank = 63
  Type = 5
  UnderTolerance = 0
  X = 71.1548
  Y = 26.1168
FEATURE [TechDraw::DrawViewDimension] Dimension010
  Arbitrary = false
  ArbitraryTolerances = false
  EqualTolerance = true
  FormatSpec = ⌀%.1f
  FormatSpecOverTolerance = %+.1f
  FormatSpecUnderTolerance = %+.1f
  Inverted = false
  LockPosition = false
  MeasureType = 1
  OverTolerance = 0
  References2D = -> [ProjItem004]
  Rotation = 0
  ScaleType = 0
  TheoreticalExact = false
  TreeRank = 65
  Type = 5
  UnderTolerance = 0
  X = 24.5151
  Y = -50.5658
FEATURE [TechDraw::DrawViewDimension] Dimension011
  Arbitrary = false
  ArbitraryTolerances = false
  EqualTolerance = true
  FormatSpec = %.1f
  FormatSpecOverTolerance = %+.1f
  FormatSpecUnderTolerance = %+.1f
  Inverted = false
  LockPosition = false
  MeasureType = 1
  OverTolerance = 0
  References2D = -> [ProjItem004]
  Rotation = 0
  ScaleType = 0
  TheoreticalExact = false
  TreeRank = 66
  Type = 1
  UnderTolerance = 0
  X = -34.341
  Y = -50.7876
FEATURE [TechDraw::DrawViewDimension] Dimension013
  Arbitrary = false
  ArbitraryTolerances = false
  EqualTolerance = true
  FormatSpec = %.1f
  FormatSpecOverTolerance = %+.1f
  FormatSpecUnderTolerance = %+.1f
  Inverted = false
  LockPosition = false
  MeasureType = 1
  OverTolerance = 0
  References2D = -> [ProjItem004]
  Rotation = 0
  ScaleType = 0
  TheoreticalExact = false
  TreeRank = 68
  Type = 0
  UnderTolerance = 0
  X = 12.7683
  Y = -13.6254
FEATURE [TechDraw::DrawViewDimension] Dimension014
  Arbitrary = false
  ArbitraryTolerances = false
  EqualTolerance = true
  FormatSpec = %.1f
  FormatSpecOverTolerance = %+.1f
  FormatSpecUnderTolerance = %+.1f
  Inverted = false
  LockPosition = false
  MeasureType = 1
  OverTolerance = 0
  References2D = -> [ProjItem005]
  Rotation = 0
  ScaleType = 0
  TheoreticalExact = false
  TreeRank = 69
  Type = 1
  UnderTolerance = 0
  X = -19.8097
  Y = -55.1967
FEATURE [TechDraw::DrawViewDimension] Dimension017
  Arbitrary = false
  ArbitraryTolerances = false
  EqualTolerance = true
  FormatSpec = ⌀%.1f
  FormatSpecOverTolerance = %+.1f
  FormatSpecUnderTolerance = %+.1f
  Inverted = false
  LockPosition = false
  MeasureType = 1
  OverTolerance = 0
  References2D = -> [ProjItem006]
  Rotation = 0
  ScaleType = 0
  TheoreticalExact = false
  TreeRank = 72
  Type = 5
  UnderTolerance = 0
  X = 62.6166
  Y = 20.895
FEATURE [TechDraw::DrawViewDimension] Dimension018
  Arbitrary = false
  ArbitraryTolerances = false
  EqualTolerance = true
  FormatSpec = %.1f
  FormatSpecOverTolerance = %+.1f
  FormatSpecUnderTolerance = %+.1f
  Inverted = false
  LockPosition = false
  MeasureType = 1
  OverTolerance = 0
  References2D = -> [ProjItem007]
  Rotation = 0
  ScaleType = 0
  TheoreticalExact = false
  TreeRank = 73
  Type = 1
  UnderTolerance = 0
  X = -26.1168
  Y = -47.7609
FEATURE [TechDraw::DrawPage] Page003
  KeepUpdated = true
  NextBalloonIndex = 1
  ProjectionType = 0
  Template = -> Template003
  TreeRank = 36
  Views = -> [ProjGroup003,Dimension017,Dimension018]
FEATURE [TechDraw::DrawViewDimension] Dimension019
  Arbitrary = false
  ArbitraryTolerances = false
  EqualTolerance = true
  FormatSpec = ⌀%.1f
  FormatSpecOverTolerance = %+.1f
  FormatSpecUnderTolerance = %+.1f
  Inverted = false
  LockPosition = false
  MeasureType = 1
  OverTolerance = 0
  References2D = -> [ProjItem008]
  Rotation = 0
  ScaleType = 0
  TheoreticalExact = false
  TreeRank = 74
  Type = 5
  UnderTolerance = 0
  X = 62.8934
  Y = 18.3883
FEATURE [TechDraw::DrawViewDimension] Dimension020
  Arbitrary = false
  ArbitraryTolerances = false
  EqualTolerance = true
  FormatSpec = ⌀%.1f
  FormatSpecOverTolerance = %+.1f
  FormatSpecUnderTolerance = %+.1f
  Inverted = false
  LockPosition = false
  MeasureType = 1
  OverTolerance = 0
  References2D = -> [ProjItem008]
  Rotation = 0
  ScaleType = 0
  TheoreticalExact = false
  TreeRank = 75
  Type = 5
  UnderTolerance = 0
  X = 64.7589
  Y = -11.7259
FEATURE [TechDraw::DrawViewDimension] Dimension021
  Arbitrary = false
  ArbitraryTolerances = false
  EqualTolerance = true
  FormatSpec = ⌀%.1f
  FormatSpecOverTolerance = %+.1f
  FormatSpecUnderTolerance = %+.1f
  Inverted = false
  LockPosition = false
  MeasureType = 1
  OverTolerance = 0
  References2D = -> [ProjItem008]
  Rotation = 0
  ScaleType = 0
  TheoreticalExact = false
  TreeRank = 76
  Type = 5
  UnderTolerance = 0
  X = 62.8934
  Y = -22.6523
FEATURE [TechDraw::DrawViewDimension] Dimension022
  Arbitrary = false
  ArbitraryTolerances = false
  EqualTolerance = true
  FormatSpec = %.1f
  FormatSpecOverTolerance = %+.1f
  FormatSpecUnderTolerance = %+.1f
  Inverted = false
  LockPosition = false
  MeasureType = 1
  OverTolerance = 0
  References2D = -> [ProjItem008]
  Rotation = 0
  ScaleType = 0
  TheoreticalExact = false
  TreeRank = 77
  Type = 7
  UnderTolerance = 0
  X = -23.8416
  Y = 18.3525
FEATURE [TechDraw::DrawViewDimension] Dimension023
  Arbitrary = false
  ArbitraryTolerances = false
  EqualTolerance = true
  FormatSpec = %.1f
  FormatSpecOverTolerance = %+.1f
  FormatSpecUnderTolerance = %+.1f
  Inverted = false
  LockPosition = false
  MeasureType = 1
  OverTolerance = 0
  References2D = -> [ProjItem009]
  Rotation = 0
  ScaleType = 0
  TheoreticalExact = false
  TreeRank = 78
  Type = 1
  UnderTolerance = 0
  X = -22.0982
  Y = -53.9275
FEATURE [TechDraw::DrawPage] Page004
  KeepUpdated = true
  NextBalloonIndex = 1
  ProjectionType = 0
  Template = -> Template004
  TreeRank = 43
  Views = -> [ProjGroup004,Dimension019,Dimension020,Dimension021,Dimension022,Dimension023]
FEATURE [TechDraw::DrawViewDimension] Dimension024
  Arbitrary = false
  ArbitraryTolerances = false
  EqualTolerance = true
  FormatSpec = ⌀%.1f
  FormatSpecOverTolerance = %+.1f
  FormatSpecUnderTolerance = %+.1f
  Inverted = false
  LockPosition = false
  MeasureType = 1
  OverTolerance = 0
  References2D = -> [ProjItem004]
  Rotation = 0
  ScaleType = 0
  TheoreticalExact = false
  TreeRank = 84
  Type = 5
  UnderTolerance = 0
  X = 56.3758
  Y = -25.651
FEATURE [TechDraw::DrawViewDimension] Dimension025
  Arbitrary = false
  ArbitraryTolerances = false
  EqualTolerance = true
  FormatSpec = %.1f
  FormatSpecOverTolerance = %+.1f
  FormatSpecUnderTolerance = %+.1f
  Inverted = false
  LockPosition = false
  MeasureType = 1
  OverTolerance = 0
  References2D = -> [ProjItem004]
  Rotation = 0
  ScaleType = 0
  TheoreticalExact = false
  TreeRank = 85
  Type = 7
  UnderTolerance = 0
  X = -24.9423
  Y = 23.4151
FEATURE [TechDraw::DrawViewDimension] Dimension026
  Arbitrary = false
  ArbitraryTolerances = false
  EqualTolerance = true
  FormatSpec = %.1f
  FormatSpecOverTolerance = %+.1f
  FormatSpecUnderTolerance = %+.1f
  Inverted = false
  LockPosition = false
  MeasureType = 1
  OverTolerance = 0
  References2D = -> [ProjItem004]
  Rotation = 0
  ScaleType = 0
  TheoreticalExact = false
  TreeRank = 86
  Type = 2
  UnderTolerance = 0
  X = 12.866
  Y = 24.4265
FEATURE [TechDraw::DrawHatch] Hatch004  label="Hatch004F0"
  HatchPattern = <path>
  Source = -> ProjItem002 [Face0]
  TreeRank = 90
FEATURE [TechDraw::DrawProjGroupItem] ProjItem012  label="Front006"
  CoarseView = false
  Direction = (0,0,-1)
  Focus = 100
  HardHidden = true
  IsoCount = 0
  IsoHidden = false
  IsoVisible = false
  LockPosition = true
  Perspective = false
  Rotation = 0
  RotationVector = (-1,0,0)
  ScaleType = 2
  SeamHidden = false
  SeamVisible = false
  SmoothHidden = false
  SmoothVisible = true
  Source = -> [Body]
  TreeRank = 92
  Type = 0
  X = 0
  XDirection = (-1,0,0)
  Y = 0
FEATURE [TechDraw::DrawProjGroupItem] ProjItem013  label="Bottom002"
  CoarseView = false
  Direction = (0,-1,0)
  Focus = 100
  HardHidden = true
  IsoCount = 0
  IsoHidden = false
  IsoVisible = false
  LockPosition = false
  Perspective = false
  Rotation = 0
  RotationVector = (1,0,0)
  ScaleType = 2
  SeamHidden = false
  SeamVisible = false
  SmoothHidden = false
  SmoothVisible = true
  Source = -> [Body]
  TreeRank = 94
  Type = 5
  X = 0
  XDirection = (-1,0,0)
  Y = 66
FEATURE [TechDraw::DrawProjGroup] ProjGroup006
  Anchor = -> ProjItem012
  AutoDistribute = true
  LockPosition = false
  ProjectionType = 0
  Rotation = 0
  ScaleType = 0
  Source = -> [Body]
  TreeRank = 93
  Views = -> [ProjItem012,ProjItem013]
  X = 153.555
  Y = 100.537
  spacingX = 15
  spacingY = 15
FEATURE [TechDraw::DrawViewDimension] Dimension028
  Arbitrary = false
  ArbitraryTolerances = false
  EqualTolerance = true
  FormatSpec = ⌀%.1f
  FormatSpecOverTolerance = %+.1f
  FormatSpecUnderTolerance = %+.1f
  Inverted = false
  LockPosition = false
  MeasureType = 1
  OverTolerance = 0
  References2D = -> [ProjItem012]
  Rotation = 0
  ScaleType = 0
  TheoreticalExact = false
  TreeRank = 95
  Type = 5
  UnderTolerance = 0
  X = 62.8934
  Y = 16.7893
FEATURE [TechDraw::DrawViewDimension] Dimension029
  Arbitrary = false
  ArbitraryTolerances = false
  EqualTolerance = true
  FormatSpec = ⌀%.1f
  FormatSpecOverTolerance = %+.1f
  FormatSpecUnderTolerance = %+.1f
  Inverted = false
  LockPosition = false
  MeasureType = 1
  OverTolerance = 0
  References2D = -> [ProjItem012]
  Rotation = 0
  ScaleType = 0
  TheoreticalExact = false
  TreeRank = 96
  Type = 5
  UnderTolerance = 0
  X = 61.8274
  Y = -14.9239
FEATURE [TechDraw::DrawViewDimension] Dimension030
  Arbitrary = false
  ArbitraryTolerances = false
  EqualTolerance = true
  FormatSpec = %.1f
  FormatSpecOverTolerance = %+.1f
  FormatSpecUnderTolerance = %+.1f
  Inverted = false
  LockPosition = false
  MeasureType = 1
  OverTolerance = 0
  References2D = -> [ProjItem013]
  Rotation = 0
  ScaleType = 0
  TheoreticalExact = false
  TreeRank = 97
  Type = 2
  UnderTolerance = 0
  X = 61.9074
  Y = -13.9278
FEATURE [TechDraw::DrawViewDimension] Dimension031
  Arbitrary = false
  ArbitraryTolerances = false
  EqualTolerance = true
  FormatSpec = %.1f
  FormatSpecOverTolerance = %+.1f
  FormatSpecUnderTolerance = %+.1f
  Inverted = false
  LockPosition = false
  MeasureType = 1
  OverTolerance = 0
  References2D = -> [ProjItem013]
  Rotation = 0
  ScaleType = 0
  TheoreticalExact = false
  TreeRank = 98
  Type = 1
  UnderTolerance = 0
  X = -32.9868
  Y = 21.5501
FEATURE [TechDraw::DrawViewDimension] Dimension032
  Arbitrary = false
  ArbitraryTolerances = false
  EqualTolerance = true
  FormatSpec = R%.1f
  FormatSpecOverTolerance = %+.1f
  FormatSpecUnderTolerance = %+.1f
  Inverted = false
  LockPosition = false
  MeasureType = 1
  OverTolerance = 0
  References2D = -> [ProjItem013]
  Rotation = 0
  ScaleType = 0
  TheoreticalExact = false
  TreeRank = 99
  Type = 4
  UnderTolerance = 0
  X = 24.0325
  Y = 21.459
FEATURE [TechDraw::DrawHatch] Hatch005  label="Hatch005F2"
  HatchPattern = <path>
  Source = -> ProjItem012 [Face2]
  TreeRank = 100
FEATURE [TechDraw::DrawHatch] Hatch  label="HatchF0"
  HatchPattern = <path>
  Source = -> ProjItem004 [Face0]
  TreeRank = 101
FEATURE [TechDraw::DrawHatch] Hatch006  label="Hatch006F0"
  HatchPattern = <path>
  Source = -> ProjItem006 [Face0]
  TreeRank = 102
FEATURE [TechDraw::DrawHatch] Hatch007  label="Hatch007F0"
  HatchPattern = <path>
  Source = -> ProjItem008 [Face0]
  TreeRank = 103
FEATURE [TechDraw::DrawHatch] Hatch008  label="Hatch008F0"
  HatchPattern = <path>
  Source = -> ProjItem010 [Face0]
  TreeRank = 104
FEATURE [TechDraw::DrawViewDimension] Dimension
  Arbitrary = false
  ArbitraryTolerances = false
  EqualTolerance = true
  FormatSpec = ⌀%.1f
  FormatSpecOverTolerance = %+.1f
  FormatSpecUnderTolerance = %+.1f
  Inverted = false
  LockPosition = false
  MeasureType = 1
  OverTolerance = 0
  References2D = -> [ProjItem010]
  Rotation = 0
  ScaleType = 0
  TheoreticalExact = false
  TreeRank = 105
  Type = 5
  UnderTolerance = 0
  X = 66.6162
  Y = -19.8953
FEATURE [TechDraw::DrawViewDimension] Dimension033
  Arbitrary = false
  ArbitraryTolerances = false
  EqualTolerance = true
  FormatSpec = ⌀%.1f
  FormatSpecOverTolerance = %+.1f
  FormatSpecUnderTolerance = %+.1f
  Inverted = false
  LockPosition = false
  MeasureType = 1
  OverTolerance = 0
  References2D = -> [ProjItem010]
  Rotation = 0
  ScaleType = 0
  TheoreticalExact = false
  TreeRank = 106
  Type = 5
  UnderTolerance = 0
  X = 64.6654
  Y = -29.0982
FEATURE [TechDraw::DrawViewDimension] Dimension034
  Arbitrary = false
  ArbitraryTolerances = false
  EqualTolerance = true
  FormatSpec = %.1f
  FormatSpecOverTolerance = %+.1f
  FormatSpecUnderTolerance = %+.1f
  Inverted = false
  LockPosition = false
  MeasureType = 1
  OverTolerance = 0
  References2D = -> [ProjItem010]
  Rotation = 0
  ScaleType = 0
  TheoreticalExact = false
  TreeRank = 107
  Type = 7
  UnderTolerance = 0
  X = -28.0652
  Y = 21.8844
FEATURE [TechDraw::DrawViewDimension] Dimension035
  Arbitrary = false
  ArbitraryTolerances = false
  EqualTolerance = true
  FormatSpec = ⌀%.1f
  FormatSpecOverTolerance = %+.1f
  FormatSpecUnderTolerance = %+.1f
  Inverted = false
  LockPosition = false
  MeasureType = 1
  OverTolerance = 0
  References2D = -> [ProjItem010]
  Rotation = 0
  ScaleType = 0
  TheoreticalExact = false
  TreeRank = 108
  Type = 5
  UnderTolerance = 0
  X = 65.5907
  Y = -39.2231
FEATURE [TechDraw::DrawViewDimension] Dimension036
  Arbitrary = false
  ArbitraryTolerances = false
  EqualTolerance = true
  FormatSpec = ⌀%.1f
  FormatSpecOverTolerance = %+.1f
  FormatSpecUnderTolerance = %+.1f
  Inverted = false
  LockPosition = false
  MeasureType = 1
  OverTolerance = 0
  References2D = -> [ProjItem010]
  Rotation = 0
  ScaleType = 0
  TheoreticalExact = false
  TreeRank = 109
  Type = 5
  UnderTolerance = 0
  X = 64.0195
  Y = 14.4713
FEATURE [TechDraw::DrawViewDimension] Dimension037
  Arbitrary = false
  ArbitraryTolerances = false
  EqualTolerance = true
  FormatSpec = ⌀%.1f
  FormatSpecOverTolerance = %+.1f
  FormatSpecUnderTolerance = %+.1f
  Inverted = false
  LockPosition = false
  MeasureType = 1
  OverTolerance = 0
  References2D = -> [ProjItem010]
  Rotation = 0
  ScaleType = 0
  TheoreticalExact = false
  TreeRank = 110
  Type = 5
  UnderTolerance = 0
  X = 35.7697
  Y = 55.2393
FEATURE [TechDraw::DrawViewDimension] Dimension038
  Arbitrary = false
  ArbitraryTolerances = false
  EqualTolerance = true
  FormatSpec = %.1f
  FormatSpecOverTolerance = %+.1f
  FormatSpecUnderTolerance = %+.1f
  Inverted = false
  LockPosition = false
  MeasureType = 1
  OverTolerance = 0
  References2D = -> [ProjItem010]
  Rotation = 0
  ScaleType = 0
  TheoreticalExact = false
  TreeRank = 111
  Type = 2
  UnderTolerance = 0
  X = 61.4452
  Y = 29.5696
FEATURE [TechDraw::DrawViewDimension] Dimension039
  Arbitrary = false
  ArbitraryTolerances = false
  EqualTolerance = true
  FormatSpec = %.1f
  FormatSpecOverTolerance = %+.1f
  FormatSpecUnderTolerance = %+.1f
  Inverted = false
  LockPosition = false
  MeasureType = 1
  OverTolerance = 0
  References2D = -> [ProjItem010]
  Rotation = 0
  ScaleType = 0
  TheoreticalExact = false
  TreeRank = 112
  Type = 2
  UnderTolerance = 0
  X = 64.9829
  Y = 5.38449
FEATURE [TechDraw::DrawViewDimension] Dimension040
  Arbitrary = false
  ArbitraryTolerances = false
  EqualTolerance = true
  FormatSpec = R%.1f
  FormatSpecOverTolerance = %+.1f
  FormatSpecUnderTolerance = %+.1f
  Inverted = false
  LockPosition = false
  MeasureType = 1
  OverTolerance = 0
  References2D = -> [ProjItem010]
  Rotation = 0
  ScaleType = 0
  TheoreticalExact = false
  TreeRank = 113
  Type = 4
  UnderTolerance = 0
  X = 15.7494
  Y = -52.0879
FEATURE [TechDraw::DrawViewDimension] Dimension041
  Arbitrary = false
  ArbitraryTolerances = false
  EqualTolerance = true
  FormatSpec = %.1f
  FormatSpecOverTolerance = %+.1f
  FormatSpecUnderTolerance = %+.1f
  Inverted = false
  LockPosition = false
  MeasureType = 1
  OverTolerance = 0
  References2D = -> [ProjItem010]
  Rotation = 0
  ScaleType = 0
  TheoreticalExact = false
  TreeRank = 114
  Type = 2
  UnderTolerance = 0
  X = 23.4221
  Y = -14.6945
FEATURE [TechDraw::DrawViewDimension] Dimension042
  Arbitrary = false
  ArbitraryTolerances = false
  EqualTolerance = true
  FormatSpec = %.1f
  FormatSpecOverTolerance = %+.1f
  FormatSpecUnderTolerance = %+.1f
  Inverted = false
  LockPosition = false
  MeasureType = 1
  OverTolerance = 0
  References2D = -> [ProjItem011]
  Rotation = 0
  ScaleType = 0
  TheoreticalExact = false
  TreeRank = 115
  Type = 1
  UnderTolerance = 0
  X = -22.2768
  Y = -58.3946
FEATURE [PartDesign::ShapeBinder] ShapeBinder012
  Placement = pos=(4e-16,-4e-16,-2.9) rot=(0,0,1;0rad)
  Support = -> [Pad006]
  TraceSupport = false
  TreeRank = 190
FEATURE [Sketcher::SketchObject] Sketch015
  ArcFitTolerance = 1e-06
  AttachmentSupport = -> [ShapeBinder012]
  ExternalGeometry = -> [ShapeBinder012]
  FullyConstrained = true
  MapMode = 5
  Placement = pos=(-3e-16,3e-16,-10.9) rot=(1,0,0;3.14159rad)
  Support = -> [ShapeBinder012]
  TreeRank = 191
  sketch-geometry (28):
    g0: LineSegment StartX=-24 StartY=5 StartZ=0 EndX=-14 EndY=5 EndZ=0
    g1: LineSegment StartX=-14 StartY=5 StartZ=0 EndX=-14 EndY=-5 EndZ=0
    g2: LineSegment StartX=-14 StartY=-5 StartZ=0 EndX=-24 EndY=-5 EndZ=0
    g3: LineSegment StartX=-24 StartY=-5 StartZ=0 EndX=-24 EndY=5 EndZ=0
    g4: LineSegment StartX=-24 StartY=19 StartZ=0 EndX=-14 EndY=19 EndZ=0
    g5: LineSegment StartX=-14 StartY=19 StartZ=0 EndX=-14 EndY=9 EndZ=0
    g6: LineSegment StartX=-14 StartY=9 StartZ=0 EndX=-24 EndY=9 EndZ=0
    g7: LineSegment StartX=-24 StartY=9 StartZ=0 EndX=-24 EndY=19 EndZ=0
    g8: LineSegment StartX=-38 StartY=5 StartZ=0 EndX=-28 EndY=5 EndZ=0
    g9: LineSegment StartX=-28 StartY=5 StartZ=0 EndX=-28 EndY=-5 EndZ=0
    g10: LineSegment StartX=-28 StartY=-5 StartZ=0 EndX=-38 EndY=-5 EndZ=0
    g11: LineSegment StartX=-38 StartY=-5 StartZ=0 EndX=-38 EndY=5 EndZ=0
    g12: LineSegment StartX=-24 StartY=-9 StartZ=0 EndX=-14 EndY=-9 EndZ=0
    g13: LineSegment StartX=-14 StartY=-9 StartZ=0 EndX=-14 EndY=-19 EndZ=0
    g14: LineSegment StartX=-14 StartY=-19 StartZ=0 EndX=-24 EndY=-19 EndZ=0
    g15: LineSegment StartX=-24 StartY=-19 StartZ=0 EndX=-24 EndY=-9 EndZ=0
    g16: LineSegment StartX=-10 StartY=5 StartZ=0 EndX=-2.13e-14 EndY=5 EndZ=0
    g17: LineSegment StartX=-2.16e-14 StartY=5 StartZ=0 EndX=-2.16e-14 EndY=-5 EndZ=0
    g18: LineSegment StartX=-2.16e-14 StartY=-5 StartZ=0 EndX=-10 EndY=-5 EndZ=0
    g19: LineSegment StartX=-10 StartY=-5 StartZ=0 EndX=-10 EndY=5 EndZ=0
    g20: LineSegment [constr] StartX=-28 StartY=5 StartZ=0 EndX=-24 EndY=5 EndZ=0
    g21: LineSegment [constr] StartX=-14 StartY=5 StartZ=0 EndX=-10 EndY=5 EndZ=0
    g22: LineSegment [constr] StartX=-24 StartY=9 StartZ=0 EndX=-24 EndY=5 EndZ=0
    g23: LineSegment [constr] StartX=-24 StartY=-5 StartZ=0 EndX=-24 EndY=-9 EndZ=0
    g24: LineSegment [constr] StartX=-19 StartY=7 StartZ=0 EndX=-19 EndY=9 EndZ=0
    g25: LineSegment [constr] StartX=-19 StartY=7 StartZ=0 EndX=-19 EndY=5 EndZ=0
    g26: LineSegment [constr] StartX=-24 StartY=-4.5e-15 StartZ=0 EndX=-26 EndY=-4.5e-15 EndZ=0
    g27: LineSegment [constr] StartX=-26 StartY=-4.5e-15 StartZ=0 EndX=-28 EndY=-4.5e-15 EndZ=0
  constraints (79):
    c: Coincident(g0,g1)
    c: Coincident(g1,g2)
    c: Coincident(g2,g3)
    c: Coincident(g3,g0)
    c: Horizontal(g0)
    c: Horizontal(g2)
    c: Vertical(g1)
    c: Coincident(g4,g5)
    c: Coincident(g5,g6)
    c: Coincident(g6,g7)
    c: Coincident(g7,g4)
    c: Horizontal(g4)
    c: Horizontal(g6)
    c: Vertical(g5)
    c: Vertical(g7)
    c: Coincident(g8,g9)
    c: Coincident(g9,g10)
    c: Coincident(g10,g11)
    c: Coincident(g11,g8)
    c: Horizontal(g8)
    c: Horizontal(g10)
    c: Vertical(g9)
    c: Vertical(g11)
    c: Coincident(g12,g13)
    c: Coincident(g13,g14)
    c: Coincident(g14,g15)
    c: Coincident(g15,g12)
    c: Horizontal(g12)
    c: Horizontal(g14)
    c: Vertical(g13)
    c: Vertical(g15)
    c: Coincident(g16,g17)
    c: Coincident(g17,g18)
    c: Coincident(g18,g19)
    c: Coincident(g19,g16)
    c: Horizontal(g16)
    c: Horizontal(g18)
    c: Vertical(g17)
    c: Vertical(g19)
    c: Equal(g13,g12)
    c: Equal(g12,g1)
    c: Equal(g1,g0)
    c: Equal(g0,g5)
    c: Equal(g5,g4)
    c: Equal(g4,g17)
    c: Equal(g17,g16)
    c: Equal(g16,g9)
    c: Equal(g9,g8)
    c: Horizontal(g8,g0)
    c: Horizontal(g0,g16)
    c: Vertical(g5,g0)
    c: Vertical(g1,g12)
    c: Coincident(g20,g8)
    c: Coincident(g20,g0)
    c: Coincident(g21,g0)
    c: Coincident(g21,g16)
    c: Coincident(g22,g6)
    c: Coincident(g22,g0)
    c: Coincident(g23,g2)
    c: Coincident(g23,g12)
    c: Equal(g23,g22)
    c: Equal(g22,g20)
    c: Equal(g20,g21)
    c: Symmetric(g0,g2,g-1)
    c: Coincident(g24,g-4)
    c: PointOnObject(g24,g6)
    c: Vertical(g24)
    c: Coincident(g25,g-4)
    c: PointOnObject(g25,g0)
    c: Vertical(g25)
    c: Equal(g25,g24)
    c: Coincident(g26,g-6)
    c: Horizontal(g26)
    c: Coincident(g27,g-6)
    c: Horizontal(g27)
    c: Equal(g27,g26)
    c: PointOnObject(g26,g3)
    c: PointOnObject(g27,g9)
    c: DistanceX(g8,g8) = 10
FEATURE [PartDesign::Pad] Pad007
  ClaimChildren = false
  Direction = (1,1,1)
  Fit = 0
  FitJoin = 0
  InnerFit = 0
  InnerFitJoin = 0
  InnerTaperAngle = 0
  InnerTaperAngleRev = 0
  Length = 0.2
  Length2 = 100
  Linearize = true
  NewSolid = false
  Placement = pos=(4e-16,-4e-16,-2.9) rot=(0,0,1;0rad)
  Profile = -> Sketch015
  Suppress = false
  TreeRank = 192
  Type = 0
  _ProfileBasedVersion = 1
FEATURE [PartDesign::Body] Body017  label="Copper_pads"
  AutoGroupSolids = false
  ClaimAllChildren = false
  ExportMode = 0
  Group = -> [ShapeBinder012,Sketch015,Pad007]
  Origin = -> Origin020
  Placement = pos=(-7.1e-15,0,3.6e-15) rot=(0,0,1;0rad)
  Tip = -> Pad007
  TreeRank = 189
  _ExportChildren = -> [ShapeBinder012,Pad007]
  _GroupVersion = 1
FEATURE [Part::Feature] trajectory_line
  TreeRank = 203
  shape: bbox 79.67 x 69 x 85 mm, 0 faces, 0 solids (baked)
FEATURE [App::DocumentObjectGroupPython] BoltGroup  # scripted group (container) (typed FeaturePython)
  AnimationStepTime = 0
  AnimationSteps = 85
  ClaimAllChildren = true
  Distance = 85
  ExportMode = 0
  Group = -> [trajectory_line]
  Revolutions = 0
  TreeRank = 223
  _GroupVersion = 1
FEATURE [Part::Feature] trajectory_line001
  TreeRank = 204
  shape: bbox 2e-07 x 2e-07 x 42 mm, 0 faces, 0 solids (baked)
FEATURE [App::DocumentObjectGroupPython] SimpleGroup  # scripted group (container) (typed FeaturePython)
  AnimationStepTime = 0
  AnimationSteps = 42
  ClaimAllChildren = true
  Distance = 42
  ExportMode = 0
  Group = -> [trajectory_line001]
  Revolutions = 0
  TreeRank = 224
  _GroupVersion = 1
FEATURE [Part::Feature] trajectory_line002
  TreeRank = 205
  shape: bbox 2e-07 x 2e-07 x 75 mm, 0 faces, 0 solids (baked)
FEATURE [App::DocumentObjectGroupPython] SimpleGroup001  # scripted group (container) (typed FeaturePython)
  AnimationStepTime = 0
  AnimationSteps = 75
  ClaimAllChildren = true
  Distance = 75
  ExportMode = 0
  Group = -> [trajectory_line002]
  Revolutions = 0
  TreeRank = 226
  _GroupVersion = 1
FEATURE [Part::Feature] trajectory_line003
  TreeRank = 206
  shape: bbox 2e-07 x 2e-07 x 35 mm, 0 faces, 0 solids (baked)
FEATURE [App::DocumentObjectGroupPython] SimpleGroup002  # scripted group (container) (typed FeaturePython)
  AnimationStepTime = 0
  AnimationSteps = 35
  ClaimAllChildren = true
  Distance = 35
  ExportMode = 0
  Group = -> [trajectory_line003]
  Revolutions = 0
  TreeRank = 227
  _GroupVersion = 1
FEATURE [Part::Feature] trajectory_line004
  TreeRank = 207
  shape: bbox 2e-07 x 2e-07 x 30 mm, 0 faces, 0 solids (baked)
FEATURE [App::DocumentObjectGroupPython] SimpleGroup003  # scripted group (container) (typed FeaturePython)
  AnimationStepTime = 0
  AnimationSteps = 30
  ClaimAllChildren = true
  Distance = 30
  ExportMode = 0
  Group = -> [trajectory_line004]
  Revolutions = 0
  TreeRank = 228
  _GroupVersion = 1
FEATURE [Part::Feature] trajectory_line005
  TreeRank = 208
  shape: bbox 2e-07 x 2e-07 x 25 mm, 0 faces, 0 solids (baked)
FEATURE [App::DocumentObjectGroupPython] SimpleGroup004  # scripted group (container) (typed FeaturePython)
  AnimationStepTime = 0
  AnimationSteps = 25
  ClaimAllChildren = true
  Distance = 25
  ExportMode = 0
  Group = -> [trajectory_line005]
  Revolutions = 0
  TreeRank = 229
  _GroupVersion = 1
FEATURE [Part::Feature] trajectory_line006
  TreeRank = 209
  shape: bbox 2e-07 x 2e-07 x 20 mm, 0 faces, 0 solids (baked)
FEATURE [App::DocumentObjectGroupPython] SimpleGroup005  # scripted group (container) (typed FeaturePython)
  AnimationStepTime = 0
  AnimationSteps = 20
  ClaimAllChildren = true
  Distance = 20
  ExportMode = 0
  Group = -> [trajectory_line006]
  Revolutions = 0
  TreeRank = 230
  _GroupVersion = 1
FEATURE [Part::Feature] trajectory_line007
  TreeRank = 201
  shape: bbox 2e-07 x 2e-07 x 20 mm, 0 faces, 0 solids (baked)
FEATURE [App::DocumentObjectGroupPython] SimpleGroup006  # scripted group (container) (typed FeaturePython)
  AnimationStepTime = 0
  AnimationSteps = 20
  ClaimAllChildren = true
  Distance = 44
  ExportMode = 0
  Group = -> [trajectory_line007]
  Revolutions = 0
  TreeRank = 225
  _GroupVersion = 0
FEATURE [App::DocumentObjectGroupPython] ExplodedAssembly  # scripted group (container) (typed FeaturePython)
  AnimationStep = 0
  ClaimAllChildren = true
  CurrentTrajectory = 0
  ExportMode = 0
  Group = -> [BoltGroup,SimpleGroup006,SimpleGroup,SimpleGroup001,SimpleGroup002,SimpleGroup003,SimpleGroup004,SimpleGroup005]
  InAnimation = false
  RemoveAllTrajectories = false
  ResetAnimation = false
  TreeRank = 231
  _GroupVersion = 0
FEATURE [TechDraw::DrawViewBalloon] Balloon
  BubbleShape = 3
  EndType = 0
  EndTypeScale = 1
  KinkLength = 5
  LockPosition = false
  OriginX = -0.585442
  OriginY = 2.42218
  Rotation = 0
  ScaleType = 0
  ShapeScale = 1
  SourceView = -> ProjItem013
  Text = Slot to allow entry for micro USB connector
  TextWrapLen = 50
  TreeRank = 232
  X = -87.7174
  Y = -30.6108
FEATURE [TechDraw::DrawPage] Page
  KeepUpdated = true
  NextBalloonIndex = 2
  ProjectionType = 0
  Template = -> Template
  TreeRank = 15
  Views = -> [ProjGroup006,Dimension028,Dimension029,Dimension030,Dimension031,Dimension032,Balloon]
FEATURE [TechDraw::DrawViewBalloon] Balloon001
  BubbleShape = 3
  EndType = 0
  EndTypeScale = 1
  KinkLength = 5
  LockPosition = false
  OriginX = -1.04631
  OriginY = -34.9651
  Rotation = 0
  ScaleType = 0
  ShapeScale = 1
  SourceView = -> ProjItem004
  Text = Slot to pass through wiring between ESP32 and LED strip
  TextWrapLen = 60
  TreeRank = 233
  X = 110.31
  Y = -44.5826
FEATURE [TechDraw::DrawPage] Page002
  KeepUpdated = true
  NextBalloonIndex = 2
  ProjectionType = 0
  Template = -> Template002
  TreeRank = 29
  Views = -> [ProjGroup002,Dimension008,Dimension010,Dimension011,Dimension013,Dimension014,Dimension024,Dimension025,Dimension026,Balloon001]
FEATURE [TechDraw::DrawViewBalloon] Balloon002
  BubbleShape = 3
  EndType = 0
  EndTypeScale = 1
  KinkLength = 5
  LockPosition = false
  OriginX = -1.11252
  OriginY = 26.2516
  Rotation = 0
  ScaleType = 0
  ShapeScale = 1
  SourceView = -> ProjItem010
  Text = Keyhole slot for wall hanging
  TextWrapLen = 60
  TreeRank = 234
  X = 93.9065
  Y = 50.3823
FEATURE [TechDraw::DrawViewBalloon] Balloon003
  BubbleShape = 3
  EndType = 0
  EndTypeScale = 1
  KinkLength = 5
  LockPosition = false
  OriginX = -0.391116
  OriginY = -34.1772
  Rotation = 0
  ScaleType = 0
  ShapeScale = 1
  SourceView = -> ProjItem010
  Text = Slot to allow micro USB connector
  TextWrapLen = 60
  TreeRank = 235
  X = 94.8944
  Y = -56.5947
FEATURE [TechDraw::DrawViewBalloon] Balloon004
  BubbleShape = 3
  EndType = 0
  EndTypeScale = 1
  KinkLength = 5
  LockPosition = false
  OriginX = -20.1563
  OriginY = -1.75334
  Rotation = 0
  ScaleType = 0
  ShapeScale = 1
  SourceView = -> ProjItem010
  Text = Holes for wire connections between ESP32 and copper touch pads on back cover
  TextWrapLen = 100
  TreeRank = 236
  X = 118.879
  Y = -9.95765
FEATURE [TechDraw::DrawPage] Page005
  KeepUpdated = true
  NextBalloonIndex = 5
  ProjectionType = 0
  Template = -> Template005
  TreeRank = 50
  Views = -> [ProjGroup005,Dimension,Dimension033,Dimension034,Dimension035,Dimension036,Dimension037,Dimension038,Dimension039,Dimension040,Dimension041,Dimension042,Balloon002,Balloon003,Balloon004]
FEATURE [App::DocumentObjectGroup] Group002  label="Fasteners"
  ClaimAllChildren = true
  ExportMode = 1
  Group = -> [Screw,Screw001,Screw002,Nut,Nut001,Nut002]
  TreeRank = 238
  _GroupVersion = 1
FEATURE [TechDraw::DrawSVGTemplate] Template006
  EditableTexts = AUTHOR_NAME=Anool J M,DRAWING_TITLE=Touch Pads,FC-DATE=02/04/2023,FC-REV=REV A,FC-SC=1:1,FC-SH=7 / 8,FC-SI=A4,FREECAD_DRAWING=Line2,Line1=Line1,+2 more (map truncated)
  Height = 210
  Orientation = 1
  TreeRank = 240
  Width = 297
FEATURE [TechDraw::DrawViewPart] View
  CoarseView = false
  Direction = (0,0,-1)
  Focus = 100
  HardHidden = true
  IsoCount = 0
  IsoHidden = false
  IsoVisible = false
  LockPosition = false
  Perspective = false
  Rotation = 0
  ScaleType = 0
  SeamHidden = false
  SeamVisible = false
  SmoothHidden = false
  SmoothVisible = true
  Source = -> [ShapeBinder012,Pad007]
  TreeRank = 248
  X = 78.9749
  XDirection = (-1,0,0)
  Y = 124.672
FEATURE [TechDraw::DrawHatch] Hatch009  label="Hatch009F5"
  HatchPattern = <path>
  Source = -> View [Face5,Face4,Face6,Face3,Face2]
  TreeRank = 249
FEATURE [TechDraw::DrawHatch] Hatch010  label="Hatch010F0"
  HatchPattern = <path>
  Source = -> View [Face0]
  TreeRank = 250
FEATURE [TechDraw::DrawViewDimension] Dimension043
  Arbitrary = false
  ArbitraryTolerances = false
  EqualTolerance = true
  FormatSpec = %.1f
  FormatSpecOverTolerance = %+.1f
  FormatSpecUnderTolerance = %+.1f
  Inverted = false
  LockPosition = false
  MeasureType = 1
  OverTolerance = 0
  References2D = -> [View]
  Rotation = 0
  ScaleType = 0
  TheoreticalExact = false
  TreeRank = 251
  Type = 1
  UnderTolerance = 0
  X = 60.5005
  Y = 28.1608
FEATURE [TechDraw::DrawViewDimension] Dimension044
  Arbitrary = false
  ArbitraryTolerances = false
  EqualTolerance = true
  FormatSpec = %.1f
  FormatSpecOverTolerance = %+.1f
  FormatSpecUnderTolerance = %+.1f
  Inverted = false
  LockPosition = false
  MeasureType = 1
  OverTolerance = 0
  References2D = -> [View]
  Rotation = 0
  ScaleType = 0
  TheoreticalExact = false
  TreeRank = 252
  Type = 2
  UnderTolerance = 0
  X = 63.2352
  Y = 16.0975
FEATURE [TechDraw::DrawViewBalloon] Balloon005
  BubbleShape = 3
  EndType = 0
  EndTypeScale = 1
  KinkLength = 5
  LockPosition = false
  OriginX = 19.3761
  OriginY = -14.7271
  Rotation = 0
  ScaleType = 0
  ShapeScale = 1
  SourceView = -> View
  Text = Adhesive copper tape touch pads, approx. 10 mm x 10 mm, 5 nos for UP / DOWN / LEFT / RIGHT / ENTER
  TextWrapLen = 100
  TreeRank = 253
  X = 125.811
  Y = -48.9134
FEATURE [TechDraw::DrawViewBalloon] Balloon006
  BubbleShape = 3
  EndType = 0
  EndTypeScale = 1
  KinkLength = 5
  LockPosition = false
  OriginX = 25.8615
  OriginY = -8.19221
  Rotation = 0
  ScaleType = 0
  ShapeScale = 1
  SourceView = -> View
  Text = Holes in back cover to pass through wires between ESP32 and copper pads
  TextWrapLen = 80
  TreeRank = 254
  X = 115.864
  Y = -28.3006
FEATURE [TechDraw::DrawPage] Page006
  KeepUpdated = true
  NextBalloonIndex = 3
  ProjectionType = 0
  Template = -> Template006
  TreeRank = 241
  Views = -> [View,Dimension043,Dimension044,Balloon005,Balloon006]
FEATURE [App::DocumentObjectGroup] Group001  label="Tech_Draw"
  ClaimAllChildren = true
  ExportMode = 1
  Group = -> [Page,Page001,Page002,Page003,Page004,Page005,Page006]
  TreeRank = 237
  _GroupVersion = 1
note: 8 file-system paths scrubbed to <path> (originals preserved in the JSON sidecar)
